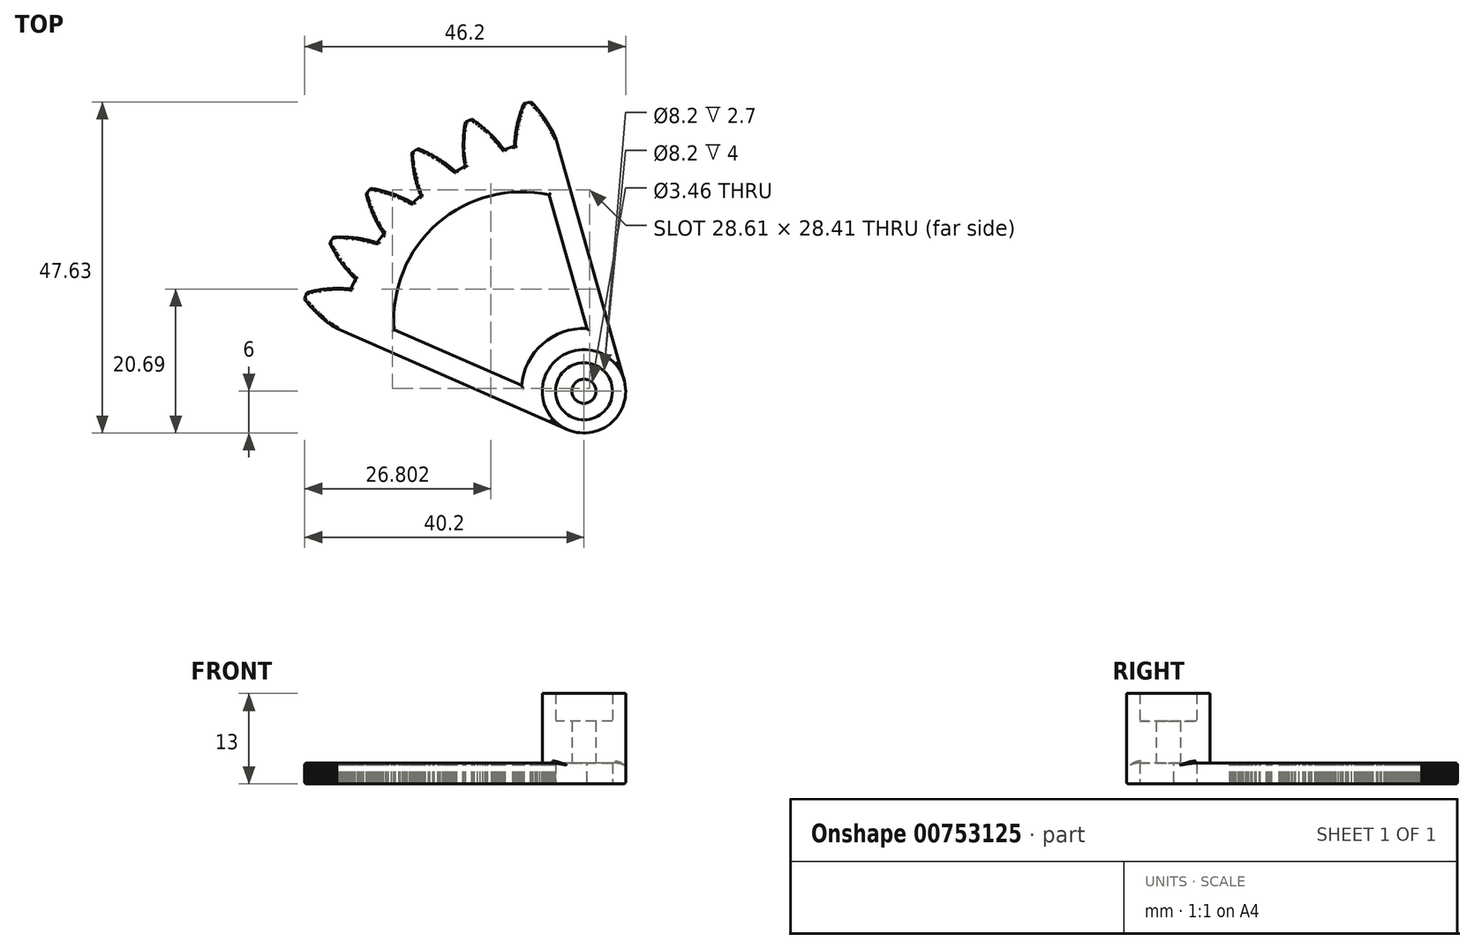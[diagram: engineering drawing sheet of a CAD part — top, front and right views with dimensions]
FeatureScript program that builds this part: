
annotation { "Feature Type Name" : "Feature", "Feature Type Description" : "" }
export const myFeature = defineFeature(function(context is Context, id is Id, definition is map)
    precondition{}
    {
        {
            var Q0;
            Q0=qCreatedBy(makeId("Top.planeOp"),FACE);
            var sketch = newSketch(context, id + "F0", { "sketchPlane" : qUnion([Q0])});
            skLineSegment(sketch, "E0", {"start": v(-4.1, 36.49) * mm, "end": v(-4.14, 36.6) * mm});
            skLineSegment(sketch, "E1", {"start": v(-4.23, 36.82) * mm, "end": v(-4.29, 36.94) * mm});
            skLineSegment(sketch, "E2", {"start": v(-4.29, 36.94) * mm, "end": v(-4.35, 37.07) * mm});
            skLineSegment(sketch, "E3", {"start": v(-4.35, 37.07) * mm, "end": v(-4.4, 37.2) * mm});
            skLineSegment(sketch, "E4", {"start": v(-4.4, 37.2) * mm, "end": v(-4.47, 37.33) * mm});
            skLineSegment(sketch, "E5", {"start": v(-4.47, 37.33) * mm, "end": v(-4.54, 37.46) * mm});
            skLineSegment(sketch, "E6", {"start": v(-4.54, 37.46) * mm, "end": v(-4.61, 37.6) * mm});
            skLineSegment(sketch, "E7", {"start": v(-4.61, 37.6) * mm, "end": v(-4.69, 37.74) * mm});
            skLineSegment(sketch, "E8", {"start": v(-4.69, 37.74) * mm, "end": v(-4.77, 37.88) * mm});
            skLineSegment(sketch, "E9", {"start": v(-4.77, 37.88) * mm, "end": v(-4.85, 38.03) * mm});
            skLineSegment(sketch, "E10", {"start": v(-4.85, 38.03) * mm, "end": v(-4.94, 38.18) * mm});
            skLineSegment(sketch, "E11", {"start": v(-4.94, 38.18) * mm, "end": v(-5.03, 38.34) * mm});
            skLineSegment(sketch, "E12", {"start": v(-5.03, 38.34) * mm, "end": v(-5.13, 38.5) * mm});
            skLineSegment(sketch, "E13", {"start": v(-5.13, 38.5) * mm, "end": v(-5.23, 38.65) * mm});
            skLineSegment(sketch, "E14", {"start": v(-5.23, 38.65) * mm, "end": v(-5.34, 38.81) * mm});
            skLineSegment(sketch, "E15", {"start": v(-5.34, 38.81) * mm, "end": v(-5.45, 38.98) * mm});
            skLineSegment(sketch, "E16", {"start": v(-5.45, 38.98) * mm, "end": v(-5.56, 39.15) * mm});
            skLineSegment(sketch, "E17", {"start": v(-5.56, 39.15) * mm, "end": v(-5.68, 39.32) * mm});
            skLineSegment(sketch, "E18", {"start": v(-5.68, 39.32) * mm, "end": v(-5.8, 39.5) * mm});
            skLineSegment(sketch, "E19", {"start": v(-5.8, 39.5) * mm, "end": v(-5.94, 39.67) * mm});
            skLineSegment(sketch, "E20", {"start": v(-5.94, 39.67) * mm, "end": v(-6.07, 39.84) * mm});
            skLineSegment(sketch, "E21", {"start": v(-6.07, 39.84) * mm, "end": v(-6.2, 40.03) * mm});
            skLineSegment(sketch, "E22", {"start": v(-6.2, 40.03) * mm, "end": v(-6.35, 40.2) * mm});
            skLineSegment(sketch, "E23", {"start": v(-6.35, 40.2) * mm, "end": v(-6.5, 40.4) * mm});
            skLineSegment(sketch, "E24", {"start": v(-6.5, 40.4) * mm, "end": v(-6.66, 40.58) * mm});
            skLineSegment(sketch, "E25", {"start": v(-6.66, 40.58) * mm, "end": v(-6.81, 40.77) * mm});
            skLineSegment(sketch, "E26", {"start": v(-6.81, 40.77) * mm, "end": v(-6.98, 40.96) * mm});
            skLineSegment(sketch, "E27", {"start": v(-6.98, 40.96) * mm, "end": v(-7.15, 41.15) * mm});
            skLineSegment(sketch, "E28", {"start": v(-7.15, 41.15) * mm, "end": v(-7.33, 41.34) * mm});
            skLineSegment(sketch, "E29", {"start": v(-7.33, 41.34) * mm, "end": v(-7.5, 41.53) * mm});
            skLineSegment(sketch, "E30", {"start": v(-7.5, 41.53) * mm, "end": v(-7.68, 41.63) * mm});
            skLineSegment(sketch, "E31", {"start": v(-7.68, 41.63) * mm, "end": v(-8.6, 41.45) * mm});
            skLineSegment(sketch, "E32", {"start": v(-8.6, 41.45) * mm, "end": v(-8.72, 41.3) * mm});
            skLineSegment(sketch, "E33", {"start": v(-8.72, 41.3) * mm, "end": v(-8.82, 41.05) * mm});
            skLineSegment(sketch, "E34", {"start": v(-8.82, 41.05) * mm, "end": v(-8.9, 40.8) * mm});
            skLineSegment(sketch, "E35", {"start": v(-8.9, 40.8) * mm, "end": v(-9, 40.56) * mm});
            skLineSegment(sketch, "E36", {"start": v(-9, 40.56) * mm, "end": v(-9.07, 40.32) * mm});
            skLineSegment(sketch, "E37", {"start": v(-9.07, 40.32) * mm, "end": v(-9.15, 40.09) * mm});
            skLineSegment(sketch, "E38", {"start": v(-9.15, 40.09) * mm, "end": v(-9.22, 39.86) * mm});
            skLineSegment(sketch, "E39", {"start": v(-9.22, 39.86) * mm, "end": v(-9.3, 39.63) * mm});
            skLineSegment(sketch, "E40", {"start": v(-9.3, 39.63) * mm, "end": v(-9.36, 39.4) * mm});
            skLineSegment(sketch, "E41", {"start": v(-9.36, 39.4) * mm, "end": v(-9.42, 39.19) * mm});
            skLineSegment(sketch, "E42", {"start": v(-9.42, 39.19) * mm, "end": v(-9.47, 38.97) * mm});
            skLineSegment(sketch, "E43", {"start": v(-9.47, 38.97) * mm, "end": v(-9.53, 38.76) * mm});
            skLineSegment(sketch, "E44", {"start": v(-9.53, 38.76) * mm, "end": v(-9.58, 38.55) * mm});
            skLineSegment(sketch, "E45", {"start": v(-9.58, 38.55) * mm, "end": v(-9.62, 38.35) * mm});
            skLineSegment(sketch, "E46", {"start": v(-9.62, 38.35) * mm, "end": v(-9.67, 38.15) * mm});
            skLineSegment(sketch, "E47", {"start": v(-9.67, 38.15) * mm, "end": v(-9.7, 37.96) * mm});
            skLineSegment(sketch, "E48", {"start": v(-9.7, 37.96) * mm, "end": v(-9.74, 37.77) * mm});
            skLineSegment(sketch, "E49", {"start": v(-9.74, 37.77) * mm, "end": v(-9.78, 37.58) * mm});
            skLineSegment(sketch, "E50", {"start": v(-9.78, 37.58) * mm, "end": v(-9.8, 37.4) * mm});
            skLineSegment(sketch, "E51", {"start": v(-9.8, 37.4) * mm, "end": v(-9.83, 37.22) * mm});
            skLineSegment(sketch, "E52", {"start": v(-9.83, 37.22) * mm, "end": v(-9.86, 37.05) * mm});
            skLineSegment(sketch, "E53", {"start": v(-9.86, 37.05) * mm, "end": v(-9.88, 36.88) * mm});
            skLineSegment(sketch, "E54", {"start": v(-9.88, 36.88) * mm, "end": v(-9.9, 36.72) * mm});
            skLineSegment(sketch, "E55", {"start": v(-9.9, 36.72) * mm, "end": v(-9.92, 36.56) * mm});
            skLineSegment(sketch, "E56", {"start": v(-9.92, 36.56) * mm, "end": v(-9.93, 36.4) * mm});
            skLineSegment(sketch, "E57", {"start": v(-9.93, 36.4) * mm, "end": v(-9.95, 36.25) * mm});
            skLineSegment(sketch, "E58", {"start": v(-9.95, 36.25) * mm, "end": v(-9.96, 36.1) * mm});
            skLineSegment(sketch, "E59", {"start": v(-9.96, 36.1) * mm, "end": v(-9.96, 35.97) * mm});
            skLineSegment(sketch, "E60", {"start": v(-9.96, 35.97) * mm, "end": v(-9.97, 35.83) * mm});
            skLineSegment(sketch, "E61", {"start": v(-9.97, 35.83) * mm, "end": v(-9.98, 35.7) * mm});
            skLineSegment(sketch, "E62", {"start": v(-9.98, 35.7) * mm, "end": v(-9.98, 35.57) * mm});
            skLineSegment(sketch, "E63", {"start": v(-9.98, 35.57) * mm, "end": v(-9.98, 35.45) * mm});
            skLineSegment(sketch, "E64", {"start": v(-9.98, 35.45) * mm, "end": v(-9.98, 35.33) * mm});
            skLineSegment(sketch, "E65", {"start": v(-9.98, 35.33) * mm, "end": v(-10.2, 35.2) * mm});
            skLineSegment(sketch, "E66", {"start": v(-10.2, 35.2) * mm, "end": v(-11.32, 34.85) * mm});
            skLineSegment(sketch, "E67", {"start": v(-11.32, 34.85) * mm, "end": v(-11.59, 34.84) * mm});
            skLineSegment(sketch, "E68", {"start": v(-11.59, 34.84) * mm, "end": v(-11.65, 34.93) * mm});
            skLineSegment(sketch, "E69", {"start": v(-11.65, 34.93) * mm, "end": v(-11.72, 35.04) * mm});
            skLineSegment(sketch, "E70", {"start": v(-11.72, 35.04) * mm, "end": v(-11.8, 35.14) * mm});
            skLineSegment(sketch, "E71", {"start": v(-11.8, 35.14) * mm, "end": v(-11.88, 35.24) * mm});
            skLineSegment(sketch, "E72", {"start": v(-11.88, 35.24) * mm, "end": v(-11.96, 35.35) * mm});
            skLineSegment(sketch, "E73", {"start": v(-11.96, 35.35) * mm, "end": v(-12.04, 35.47) * mm});
            skLineSegment(sketch, "E74", {"start": v(-12.04, 35.47) * mm, "end": v(-12.14, 35.58) * mm});
            skLineSegment(sketch, "E75", {"start": v(-12.14, 35.58) * mm, "end": v(-12.23, 35.7) * mm});
            skLineSegment(sketch, "E76", {"start": v(-12.23, 35.7) * mm, "end": v(-12.33, 35.82) * mm});
            skLineSegment(sketch, "E77", {"start": v(-12.33, 35.82) * mm, "end": v(-12.43, 35.94) * mm});
            skLineSegment(sketch, "E78", {"start": v(-12.43, 35.94) * mm, "end": v(-12.54, 36.06) * mm});
            skLineSegment(sketch, "E79", {"start": v(-12.54, 36.06) * mm, "end": v(-12.65, 36.2) * mm});
            skLineSegment(sketch, "E80", {"start": v(-12.65, 36.2) * mm, "end": v(-12.77, 36.32) * mm});
            skLineSegment(sketch, "E81", {"start": v(-12.77, 36.32) * mm, "end": v(-12.9, 36.45) * mm});
            skLineSegment(sketch, "E82", {"start": v(-12.9, 36.45) * mm, "end": v(-13.02, 36.58) * mm});
            skLineSegment(sketch, "E83", {"start": v(-13.02, 36.58) * mm, "end": v(-13.15, 36.72) * mm});
            skLineSegment(sketch, "E84", {"start": v(-13.15, 36.72) * mm, "end": v(-13.3, 36.86) * mm});
            skLineSegment(sketch, "E85", {"start": v(-13.3, 36.86) * mm, "end": v(-13.43, 37) * mm});
            skLineSegment(sketch, "E86", {"start": v(-13.43, 37) * mm, "end": v(-13.58, 37.14) * mm});
            skLineSegment(sketch, "E87", {"start": v(-13.58, 37.14) * mm, "end": v(-13.73, 37.28) * mm});
            skLineSegment(sketch, "E88", {"start": v(-13.73, 37.28) * mm, "end": v(-13.89, 37.42) * mm});
            skLineSegment(sketch, "E89", {"start": v(-13.89, 37.42) * mm, "end": v(-14.05, 37.57) * mm});
            skLineSegment(sketch, "E90", {"start": v(-14.05, 37.57) * mm, "end": v(-14.22, 37.71) * mm});
            skLineSegment(sketch, "E91", {"start": v(-14.22, 37.71) * mm, "end": v(-14.4, 37.86) * mm});
            skLineSegment(sketch, "E92", {"start": v(-14.4, 37.86) * mm, "end": v(-14.57, 38) * mm});
            skLineSegment(sketch, "E93", {"start": v(-14.57, 38) * mm, "end": v(-14.76, 38.16) * mm});
            skLineSegment(sketch, "E94", {"start": v(-14.76, 38.16) * mm, "end": v(-14.95, 38.3) * mm});
            skLineSegment(sketch, "E95", {"start": v(-14.95, 38.3) * mm, "end": v(-15.14, 38.46) * mm});
            skLineSegment(sketch, "E96", {"start": v(-15.14, 38.46) * mm, "end": v(-15.34, 38.6) * mm});
            skLineSegment(sketch, "E97", {"start": v(-15.34, 38.6) * mm, "end": v(-15.55, 38.76) * mm});
            skLineSegment(sketch, "E98", {"start": v(-15.55, 38.76) * mm, "end": v(-15.76, 38.91) * mm});
            skLineSegment(sketch, "E99", {"start": v(-15.76, 38.91) * mm, "end": v(-15.98, 39.06) * mm});
            skLineSegment(sketch, "E100", {"start": v(-15.98, 39.06) * mm, "end": v(-16.16, 39.13) * mm});
            skLineSegment(sketch, "E101", {"start": v(-16.16, 39.13) * mm, "end": v(-17.03, 38.75) * mm});
            skLineSegment(sketch, "E102", {"start": v(-17.03, 38.75) * mm, "end": v(-17.12, 38.58) * mm});
            skLineSegment(sketch, "E103", {"start": v(-17.12, 38.58) * mm, "end": v(-17.16, 38.32) * mm});
            skLineSegment(sketch, "E104", {"start": v(-17.16, 38.32) * mm, "end": v(-17.2, 38.06) * mm});
            skLineSegment(sketch, "E105", {"start": v(-17.2, 38.06) * mm, "end": v(-17.23, 37.8) * mm});
            skLineSegment(sketch, "E106", {"start": v(-17.23, 37.8) * mm, "end": v(-17.26, 37.55) * mm});
            skLineSegment(sketch, "E107", {"start": v(-17.26, 37.55) * mm, "end": v(-17.29, 37.3) * mm});
            skLineSegment(sketch, "E108", {"start": v(-17.29, 37.3) * mm, "end": v(-17.3, 37.07) * mm});
            skLineSegment(sketch, "E109", {"start": v(-17.3, 37.07) * mm, "end": v(-17.33, 36.83) * mm});
            skLineSegment(sketch, "E110", {"start": v(-17.33, 36.83) * mm, "end": v(-17.35, 36.6) * mm});
            skLineSegment(sketch, "E111", {"start": v(-17.35, 36.6) * mm, "end": v(-17.36, 36.37) * mm});
            skLineSegment(sketch, "E112", {"start": v(-17.36, 36.37) * mm, "end": v(-17.37, 36.15) * mm});
            skLineSegment(sketch, "E113", {"start": v(-17.37, 36.15) * mm, "end": v(-17.38, 35.93) * mm});
            skLineSegment(sketch, "E114", {"start": v(-17.38, 35.93) * mm, "end": v(-17.38, 35.72) * mm});
            skLineSegment(sketch, "E115", {"start": v(-17.38, 35.72) * mm, "end": v(-17.39, 35.51) * mm});
            skLineSegment(sketch, "E116", {"start": v(-17.39, 35.51) * mm, "end": v(-17.39, 35.3) * mm});
            skLineSegment(sketch, "E117", {"start": v(-17.39, 35.3) * mm, "end": v(-17.39, 35.11) * mm});
            skLineSegment(sketch, "E118", {"start": v(-17.39, 35.11) * mm, "end": v(-17.38, 34.92) * mm});
            skLineSegment(sketch, "E119", {"start": v(-17.38, 34.92) * mm, "end": v(-17.38, 34.73) * mm});
            skLineSegment(sketch, "E120", {"start": v(-17.38, 34.73) * mm, "end": v(-17.37, 34.54) * mm});
            skLineSegment(sketch, "E121", {"start": v(-17.37, 34.54) * mm, "end": v(-17.36, 34.36) * mm});
            skLineSegment(sketch, "E122", {"start": v(-17.36, 34.36) * mm, "end": v(-17.35, 34.2) * mm});
            skLineSegment(sketch, "E123", {"start": v(-17.35, 34.2) * mm, "end": v(-17.33, 34.02) * mm});
            skLineSegment(sketch, "E124", {"start": v(-17.33, 34.02) * mm, "end": v(-17.32, 33.86) * mm});
            skLineSegment(sketch, "E125", {"start": v(-17.32, 33.86) * mm, "end": v(-17.3, 33.7) * mm});
            skLineSegment(sketch, "E126", {"start": v(-17.3, 33.7) * mm, "end": v(-17.28, 33.54) * mm});
            skLineSegment(sketch, "E127", {"start": v(-17.28, 33.54) * mm, "end": v(-17.27, 33.4) * mm});
            skLineSegment(sketch, "E128", {"start": v(-17.27, 33.4) * mm, "end": v(-17.25, 33.25) * mm});
            skLineSegment(sketch, "E129", {"start": v(-17.25, 33.25) * mm, "end": v(-17.22, 33.1) * mm});
            skLineSegment(sketch, "E130", {"start": v(-17.22, 33.1) * mm, "end": v(-17.2, 32.97) * mm});
            skLineSegment(sketch, "E131", {"start": v(-17.2, 32.97) * mm, "end": v(-17.18, 32.84) * mm});
            skLineSegment(sketch, "E132", {"start": v(-17.18, 32.84) * mm, "end": v(-17.16, 32.72) * mm});
            skLineSegment(sketch, "E133", {"start": v(-17.16, 32.72) * mm, "end": v(-17.13, 32.6) * mm});
            skLineSegment(sketch, "E134", {"start": v(-17.13, 32.6) * mm, "end": v(-17.1, 32.48) * mm});
            skLineSegment(sketch, "E135", {"start": v(-17.1, 32.48) * mm, "end": v(-17.3, 32.3) * mm});
            skLineSegment(sketch, "E136", {"start": v(-17.3, 32.3) * mm, "end": v(-18.32, 31.73) * mm});
            skLineSegment(sketch, "E137", {"start": v(-18.32, 31.73) * mm, "end": v(-18.58, 31.67) * mm});
            skLineSegment(sketch, "E138", {"start": v(-18.58, 31.67) * mm, "end": v(-18.66, 31.75) * mm});
            skLineSegment(sketch, "E139", {"start": v(-18.66, 31.75) * mm, "end": v(-18.75, 31.83) * mm});
            skLineSegment(sketch, "E140", {"start": v(-18.75, 31.83) * mm, "end": v(-18.85, 31.92) * mm});
            skLineSegment(sketch, "E141", {"start": v(-18.85, 31.92) * mm, "end": v(-18.94, 32) * mm});
            skLineSegment(sketch, "E142", {"start": v(-18.94, 32) * mm, "end": v(-19.05, 32.1) * mm});
            skLineSegment(sketch, "E143", {"start": v(-19.05, 32.1) * mm, "end": v(-19.15, 32.19) * mm});
            skLineSegment(sketch, "E144", {"start": v(-19.15, 32.19) * mm, "end": v(-19.27, 32.28) * mm});
            skLineSegment(sketch, "E145", {"start": v(-19.27, 32.28) * mm, "end": v(-19.38, 32.37) * mm});
            skLineSegment(sketch, "E146", {"start": v(-19.38, 32.37) * mm, "end": v(-19.5, 32.47) * mm});
            skLineSegment(sketch, "E147", {"start": v(-19.5, 32.47) * mm, "end": v(-19.63, 32.57) * mm});
            skLineSegment(sketch, "E148", {"start": v(-19.63, 32.57) * mm, "end": v(-19.77, 32.67) * mm});
            skLineSegment(sketch, "E149", {"start": v(-19.77, 32.67) * mm, "end": v(-19.9, 32.77) * mm});
            skLineSegment(sketch, "E150", {"start": v(-19.9, 32.77) * mm, "end": v(-20.04, 32.87) * mm});
            skLineSegment(sketch, "E151", {"start": v(-20.04, 32.87) * mm, "end": v(-20.2, 32.97) * mm});
            skLineSegment(sketch, "E152", {"start": v(-20.2, 32.97) * mm, "end": v(-20.34, 33.08) * mm});
            skLineSegment(sketch, "E153", {"start": v(-20.34, 33.08) * mm, "end": v(-20.5, 33.18) * mm});
            skLineSegment(sketch, "E154", {"start": v(-20.5, 33.18) * mm, "end": v(-20.66, 33.29) * mm});
            skLineSegment(sketch, "E155", {"start": v(-20.66, 33.29) * mm, "end": v(-20.83, 33.4) * mm});
            skLineSegment(sketch, "E156", {"start": v(-20.83, 33.4) * mm, "end": v(-21, 33.5) * mm});
            skLineSegment(sketch, "E157", {"start": v(-21, 33.5) * mm, "end": v(-21.18, 33.6) * mm});
            skLineSegment(sketch, "E158", {"start": v(-21.18, 33.6) * mm, "end": v(-21.37, 33.72) * mm});
            skLineSegment(sketch, "E159", {"start": v(-21.37, 33.72) * mm, "end": v(-21.56, 33.82) * mm});
            skLineSegment(sketch, "E160", {"start": v(-21.56, 33.82) * mm, "end": v(-21.75, 33.93) * mm});
            skLineSegment(sketch, "E161", {"start": v(-21.75, 33.93) * mm, "end": v(-21.95, 34.04) * mm});
            skLineSegment(sketch, "E162", {"start": v(-21.95, 34.04) * mm, "end": v(-22.16, 34.15) * mm});
            skLineSegment(sketch, "E163", {"start": v(-22.16, 34.15) * mm, "end": v(-22.37, 34.26) * mm});
            skLineSegment(sketch, "E164", {"start": v(-22.37, 34.26) * mm, "end": v(-22.58, 34.36) * mm});
            skLineSegment(sketch, "E165", {"start": v(-22.58, 34.36) * mm, "end": v(-22.8, 34.47) * mm});
            skLineSegment(sketch, "E166", {"start": v(-22.8, 34.47) * mm, "end": v(-23.03, 34.58) * mm});
            skLineSegment(sketch, "E167", {"start": v(-23.03, 34.58) * mm, "end": v(-23.27, 34.68) * mm});
            skLineSegment(sketch, "E168", {"start": v(-23.27, 34.68) * mm, "end": v(-23.5, 34.79) * mm});
            skLineSegment(sketch, "E169", {"start": v(-23.5, 34.79) * mm, "end": v(-23.75, 34.89) * mm});
            skLineSegment(sketch, "E170", {"start": v(-23.75, 34.89) * mm, "end": v(-23.94, 34.9) * mm});
            skLineSegment(sketch, "E171", {"start": v(-23.94, 34.9) * mm, "end": v(-24.72, 34.37) * mm});
            skLineSegment(sketch, "E172", {"start": v(-24.72, 34.37) * mm, "end": v(-24.76, 34.18) * mm});
            skLineSegment(sketch, "E173", {"start": v(-24.76, 34.18) * mm, "end": v(-24.75, 33.91) * mm});
            skLineSegment(sketch, "E174", {"start": v(-24.75, 33.91) * mm, "end": v(-24.73, 33.65) * mm});
            skLineSegment(sketch, "E175", {"start": v(-24.73, 33.65) * mm, "end": v(-24.71, 33.4) * mm});
            skLineSegment(sketch, "E176", {"start": v(-24.71, 33.4) * mm, "end": v(-24.7, 33.15) * mm});
            skLineSegment(sketch, "E177", {"start": v(-24.7, 33.15) * mm, "end": v(-24.67, 32.9) * mm});
            skLineSegment(sketch, "E178", {"start": v(-24.67, 32.9) * mm, "end": v(-24.64, 32.66) * mm});
            skLineSegment(sketch, "E179", {"start": v(-24.64, 32.66) * mm, "end": v(-24.6, 32.43) * mm});
            skLineSegment(sketch, "E180", {"start": v(-24.6, 32.43) * mm, "end": v(-24.58, 32.2) * mm});
            skLineSegment(sketch, "E181", {"start": v(-24.58, 32.2) * mm, "end": v(-24.54, 31.97) * mm});
            skLineSegment(sketch, "E182", {"start": v(-24.54, 31.97) * mm, "end": v(-24.5, 31.75) * mm});
            skLineSegment(sketch, "E183", {"start": v(-24.5, 31.75) * mm, "end": v(-24.47, 31.54) * mm});
            skLineSegment(sketch, "E184", {"start": v(-24.47, 31.54) * mm, "end": v(-24.43, 31.33) * mm});
            skLineSegment(sketch, "E185", {"start": v(-24.43, 31.33) * mm, "end": v(-24.4, 31.12) * mm});
            skLineSegment(sketch, "E186", {"start": v(-24.4, 31.12) * mm, "end": v(-24.35, 30.92) * mm});
            skLineSegment(sketch, "E187", {"start": v(-24.35, 30.92) * mm, "end": v(-24.3, 30.73) * mm});
            skLineSegment(sketch, "E188", {"start": v(-24.3, 30.73) * mm, "end": v(-24.26, 30.54) * mm});
            skLineSegment(sketch, "E189", {"start": v(-24.26, 30.54) * mm, "end": v(-24.22, 30.36) * mm});
            skLineSegment(sketch, "E190", {"start": v(-24.22, 30.36) * mm, "end": v(-24.17, 30.18) * mm});
            skLineSegment(sketch, "E191", {"start": v(-24.17, 30.18) * mm, "end": v(-24.12, 30) * mm});
            skLineSegment(sketch, "E192", {"start": v(-24.12, 30) * mm, "end": v(-24.08, 29.84) * mm});
            skLineSegment(sketch, "E193", {"start": v(-24.08, 29.84) * mm, "end": v(-24.03, 29.67) * mm});
            skLineSegment(sketch, "E194", {"start": v(-24.03, 29.67) * mm, "end": v(-23.98, 29.52) * mm});
            skLineSegment(sketch, "E195", {"start": v(-23.98, 29.52) * mm, "end": v(-23.93, 29.36) * mm});
            skLineSegment(sketch, "E196", {"start": v(-23.93, 29.36) * mm, "end": v(-23.88, 29.22) * mm});
            skLineSegment(sketch, "E197", {"start": v(-23.88, 29.22) * mm, "end": v(-23.83, 29.07) * mm});
            skLineSegment(sketch, "E198", {"start": v(-23.83, 29.07) * mm, "end": v(-23.78, 28.94) * mm});
            skLineSegment(sketch, "E199", {"start": v(-23.78, 28.94) * mm, "end": v(-23.73, 28.8) * mm});
            skLineSegment(sketch, "E200", {"start": v(-23.73, 28.8) * mm, "end": v(-23.68, 28.68) * mm});
            skLineSegment(sketch, "E201", {"start": v(-23.68, 28.68) * mm, "end": v(-23.63, 28.55) * mm});
            skLineSegment(sketch, "E202", {"start": v(-23.63, 28.55) * mm, "end": v(-23.59, 28.44) * mm});
            skLineSegment(sketch, "E203", {"start": v(-23.59, 28.44) * mm, "end": v(-23.54, 28.32) * mm});
            skLineSegment(sketch, "E204", {"start": v(-23.54, 28.32) * mm, "end": v(-23.5, 28.22) * mm});
            skLineSegment(sketch, "E205", {"start": v(-23.5, 28.22) * mm, "end": v(-23.64, 28) * mm});
            skLineSegment(sketch, "E206", {"start": v(-23.64, 28) * mm, "end": v(-24.52, 27.23) * mm});
            skLineSegment(sketch, "E207", {"start": v(-24.52, 27.23) * mm, "end": v(-24.76, 27.11) * mm});
            skLineSegment(sketch, "E208", {"start": v(-24.76, 27.11) * mm, "end": v(-24.86, 27.17) * mm});
            skLineSegment(sketch, "E209", {"start": v(-24.86, 27.17) * mm, "end": v(-24.96, 27.24) * mm});
            skLineSegment(sketch, "E210", {"start": v(-24.96, 27.24) * mm, "end": v(-25.07, 27.3) * mm});
            skLineSegment(sketch, "E211", {"start": v(-25.07, 27.3) * mm, "end": v(-25.18, 27.37) * mm});
            skLineSegment(sketch, "E212", {"start": v(-25.18, 27.37) * mm, "end": v(-25.3, 27.43) * mm});
            skLineSegment(sketch, "E213", {"start": v(-25.3, 27.43) * mm, "end": v(-25.43, 27.5) * mm});
            skLineSegment(sketch, "E214", {"start": v(-25.43, 27.5) * mm, "end": v(-25.56, 27.57) * mm});
            skLineSegment(sketch, "E215", {"start": v(-25.56, 27.57) * mm, "end": v(-25.7, 27.64) * mm});
            skLineSegment(sketch, "E216", {"start": v(-25.7, 27.64) * mm, "end": v(-25.83, 27.7) * mm});
            skLineSegment(sketch, "E217", {"start": v(-25.83, 27.7) * mm, "end": v(-25.98, 27.77) * mm});
            skLineSegment(sketch, "E218", {"start": v(-25.98, 27.77) * mm, "end": v(-26.12, 27.84) * mm});
            skLineSegment(sketch, "E219", {"start": v(-26.12, 27.84) * mm, "end": v(-26.28, 27.91) * mm});
            skLineSegment(sketch, "E220", {"start": v(-26.28, 27.91) * mm, "end": v(-26.44, 27.99) * mm});
            skLineSegment(sketch, "E221", {"start": v(-26.44, 27.99) * mm, "end": v(-26.6, 28.06) * mm});
            skLineSegment(sketch, "E222", {"start": v(-26.6, 28.06) * mm, "end": v(-26.78, 28.12) * mm});
            skLineSegment(sketch, "E223", {"start": v(-26.78, 28.12) * mm, "end": v(-26.95, 28.2) * mm});
            skLineSegment(sketch, "E224", {"start": v(-26.95, 28.2) * mm, "end": v(-27.13, 28.26) * mm});
            skLineSegment(sketch, "E225", {"start": v(-27.13, 28.26) * mm, "end": v(-27.32, 28.33) * mm});
            skLineSegment(sketch, "E226", {"start": v(-27.32, 28.33) * mm, "end": v(-27.5, 28.4) * mm});
            skLineSegment(sketch, "E227", {"start": v(-27.5, 28.4) * mm, "end": v(-27.7, 28.47) * mm});
            skLineSegment(sketch, "E228", {"start": v(-27.7, 28.47) * mm, "end": v(-27.9, 28.54) * mm});
            skLineSegment(sketch, "E229", {"start": v(-27.9, 28.54) * mm, "end": v(-28.12, 28.6) * mm});
            skLineSegment(sketch, "E230", {"start": v(-28.12, 28.6) * mm, "end": v(-28.33, 28.67) * mm});
            skLineSegment(sketch, "E231", {"start": v(-28.33, 28.67) * mm, "end": v(-28.55, 28.73) * mm});
            skLineSegment(sketch, "E232", {"start": v(-28.55, 28.73) * mm, "end": v(-28.77, 28.8) * mm});
            skLineSegment(sketch, "E233", {"start": v(-28.77, 28.8) * mm, "end": v(-29, 28.86) * mm});
            skLineSegment(sketch, "E234", {"start": v(-29, 28.86) * mm, "end": v(-29.24, 28.92) * mm});
            skLineSegment(sketch, "E235", {"start": v(-29.24, 28.92) * mm, "end": v(-29.47, 28.97) * mm});
            skLineSegment(sketch, "E236", {"start": v(-29.47, 28.97) * mm, "end": v(-29.72, 29.03) * mm});
            skLineSegment(sketch, "E237", {"start": v(-29.72, 29.03) * mm, "end": v(-29.97, 29.08) * mm});
            skLineSegment(sketch, "E238", {"start": v(-29.97, 29.08) * mm, "end": v(-30.22, 29.14) * mm});
            skLineSegment(sketch, "E239", {"start": v(-30.22, 29.14) * mm, "end": v(-30.49, 29.19) * mm});
            skLineSegment(sketch, "E240", {"start": v(-30.49, 29.19) * mm, "end": v(-30.68, 29.17) * mm});
            skLineSegment(sketch, "E241", {"start": v(-30.68, 29.17) * mm, "end": v(-31.32, 28.48) * mm});
            skLineSegment(sketch, "E242", {"start": v(-31.32, 28.48) * mm, "end": v(-31.33, 28.28) * mm});
            skLineSegment(sketch, "E243", {"start": v(-31.33, 28.28) * mm, "end": v(-31.26, 28.02) * mm});
            skLineSegment(sketch, "E244", {"start": v(-31.26, 28.02) * mm, "end": v(-31.19, 27.77) * mm});
            skLineSegment(sketch, "E245", {"start": v(-31.19, 27.77) * mm, "end": v(-31.12, 27.53) * mm});
            skLineSegment(sketch, "E246", {"start": v(-31.12, 27.53) * mm, "end": v(-31.04, 27.29) * mm});
            skLineSegment(sketch, "E247", {"start": v(-31.04, 27.29) * mm, "end": v(-30.97, 27.05) * mm});
            skLineSegment(sketch, "E248", {"start": v(-30.97, 27.05) * mm, "end": v(-30.9, 26.82) * mm});
            skLineSegment(sketch, "E249", {"start": v(-30.9, 26.82) * mm, "end": v(-30.81, 26.6) * mm});
            skLineSegment(sketch, "E250", {"start": v(-30.81, 26.6) * mm, "end": v(-30.73, 26.38) * mm});
            skLineSegment(sketch, "E251", {"start": v(-30.73, 26.38) * mm, "end": v(-30.65, 26.17) * mm});
            skLineSegment(sketch, "E252", {"start": v(-30.65, 26.17) * mm, "end": v(-30.57, 25.96) * mm});
            skLineSegment(sketch, "E253", {"start": v(-30.57, 25.96) * mm, "end": v(-30.5, 25.76) * mm});
            skLineSegment(sketch, "E254", {"start": v(-30.5, 25.76) * mm, "end": v(-30.41, 25.56) * mm});
            skLineSegment(sketch, "E255", {"start": v(-30.41, 25.56) * mm, "end": v(-30.33, 25.37) * mm});
            skLineSegment(sketch, "E256", {"start": v(-30.33, 25.37) * mm, "end": v(-30.25, 25.19) * mm});
            skLineSegment(sketch, "E257", {"start": v(-30.25, 25.19) * mm, "end": v(-30.16, 25) * mm});
            skLineSegment(sketch, "E258", {"start": v(-30.16, 25) * mm, "end": v(-30.08, 24.83) * mm});
            skLineSegment(sketch, "E259", {"start": v(-30.08, 24.83) * mm, "end": v(-30, 24.66) * mm});
            skLineSegment(sketch, "E260", {"start": v(-30, 24.66) * mm, "end": v(-29.92, 24.5) * mm});
            skLineSegment(sketch, "E261", {"start": v(-29.92, 24.5) * mm, "end": v(-29.83, 24.33) * mm});
            skLineSegment(sketch, "E262", {"start": v(-29.83, 24.33) * mm, "end": v(-29.75, 24.18) * mm});
            skLineSegment(sketch, "E263", {"start": v(-29.75, 24.18) * mm, "end": v(-29.67, 24.03) * mm});
            skLineSegment(sketch, "E264", {"start": v(-29.67, 24.03) * mm, "end": v(-29.6, 23.89) * mm});
            skLineSegment(sketch, "E265", {"start": v(-29.6, 23.89) * mm, "end": v(-29.51, 23.75) * mm});
            skLineSegment(sketch, "E266", {"start": v(-29.51, 23.75) * mm, "end": v(-29.43, 23.61) * mm});
            skLineSegment(sketch, "E267", {"start": v(-29.43, 23.61) * mm, "end": v(-29.36, 23.48) * mm});
            skLineSegment(sketch, "E268", {"start": v(-29.36, 23.48) * mm, "end": v(-29.28, 23.36) * mm});
            skLineSegment(sketch, "E269", {"start": v(-29.28, 23.36) * mm, "end": v(-29.2, 23.24) * mm});
            skLineSegment(sketch, "E270", {"start": v(-29.2, 23.24) * mm, "end": v(-29.13, 23.13) * mm});
            skLineSegment(sketch, "E271", {"start": v(-29.13, 23.13) * mm, "end": v(-29.05, 23.02) * mm});
            skLineSegment(sketch, "E272", {"start": v(-29.05, 23.02) * mm, "end": v(-28.98, 22.91) * mm});
            skLineSegment(sketch, "E273", {"start": v(-28.98, 22.91) * mm, "end": v(-28.91, 22.81) * mm});
            skLineSegment(sketch, "E274", {"start": v(-28.91, 22.81) * mm, "end": v(-28.84, 22.72) * mm});
            skLineSegment(sketch, "E275", {"start": v(-28.84, 22.72) * mm, "end": v(-28.94, 22.47) * mm});
            skLineSegment(sketch, "E276", {"start": v(-28.94, 22.47) * mm, "end": v(-29.65, 21.54) * mm});
            skLineSegment(sketch, "E277", {"start": v(-29.65, 21.54) * mm, "end": v(-29.85, 21.37) * mm});
            skLineSegment(sketch, "E278", {"start": v(-29.85, 21.37) * mm, "end": v(-29.96, 21.41) * mm});
            skLineSegment(sketch, "E279", {"start": v(-29.96, 21.41) * mm, "end": v(-30.08, 21.45) * mm});
            skLineSegment(sketch, "E280", {"start": v(-30.08, 21.45) * mm, "end": v(-30.2, 21.5) * mm});
            skLineSegment(sketch, "E281", {"start": v(-30.2, 21.5) * mm, "end": v(-30.32, 21.53) * mm});
            skLineSegment(sketch, "E282", {"start": v(-30.32, 21.53) * mm, "end": v(-30.45, 21.57) * mm});
            skLineSegment(sketch, "E283", {"start": v(-30.45, 21.57) * mm, "end": v(-30.59, 21.61) * mm});
            skLineSegment(sketch, "E284", {"start": v(-30.59, 21.61) * mm, "end": v(-30.73, 21.65) * mm});
            skLineSegment(sketch, "E285", {"start": v(-30.73, 21.65) * mm, "end": v(-30.88, 21.7) * mm});
            skLineSegment(sketch, "E286", {"start": v(-30.88, 21.7) * mm, "end": v(-31.03, 21.73) * mm});
            skLineSegment(sketch, "E287", {"start": v(-31.03, 21.73) * mm, "end": v(-31.18, 21.77) * mm});
            skLineSegment(sketch, "E288", {"start": v(-31.18, 21.77) * mm, "end": v(-31.34, 21.8) * mm});
            skLineSegment(sketch, "E289", {"start": v(-31.34, 21.8) * mm, "end": v(-31.5, 21.84) * mm});
            skLineSegment(sketch, "E290", {"start": v(-31.5, 21.84) * mm, "end": v(-31.68, 21.88) * mm});
            skLineSegment(sketch, "E291", {"start": v(-31.68, 21.88) * mm, "end": v(-31.86, 21.91) * mm});
            skLineSegment(sketch, "E292", {"start": v(-31.86, 21.91) * mm, "end": v(-32.04, 21.94) * mm});
            skLineSegment(sketch, "E293", {"start": v(-32.04, 21.94) * mm, "end": v(-32.22, 21.98) * mm});
            skLineSegment(sketch, "E294", {"start": v(-32.22, 21.98) * mm, "end": v(-32.42, 22) * mm});
            skLineSegment(sketch, "E295", {"start": v(-32.42, 22) * mm, "end": v(-32.61, 22.03) * mm});
            skLineSegment(sketch, "E296", {"start": v(-32.61, 22.03) * mm, "end": v(-32.81, 22.06) * mm});
            skLineSegment(sketch, "E297", {"start": v(-32.81, 22.06) * mm, "end": v(-33.02, 22.09) * mm});
            skLineSegment(sketch, "E298", {"start": v(-33.02, 22.09) * mm, "end": v(-33.23, 22.11) * mm});
            skLineSegment(sketch, "E299", {"start": v(-33.23, 22.11) * mm, "end": v(-33.45, 22.13) * mm});
            skLineSegment(sketch, "E300", {"start": v(-33.45, 22.13) * mm, "end": v(-33.67, 22.15) * mm});
            skLineSegment(sketch, "E301", {"start": v(-33.67, 22.15) * mm, "end": v(-33.9, 22.17) * mm});
            skLineSegment(sketch, "E302", {"start": v(-33.9, 22.17) * mm, "end": v(-34.13, 22.18) * mm});
            skLineSegment(sketch, "E303", {"start": v(-34.13, 22.18) * mm, "end": v(-34.37, 22.2) * mm});
            skLineSegment(sketch, "E304", {"start": v(-34.37, 22.2) * mm, "end": v(-34.6, 22.2) * mm});
            skLineSegment(sketch, "E305", {"start": v(-34.6, 22.2) * mm, "end": v(-34.85, 22.21) * mm});
            skLineSegment(sketch, "E306", {"start": v(-34.85, 22.21) * mm, "end": v(-35.1, 22.22) * mm});
            skLineSegment(sketch, "E307", {"start": v(-35.1, 22.22) * mm, "end": v(-35.36, 22.22) * mm});
            skLineSegment(sketch, "E308", {"start": v(-35.36, 22.22) * mm, "end": v(-35.62, 22.22) * mm});
            skLineSegment(sketch, "E309", {"start": v(-35.62, 22.22) * mm, "end": v(-35.89, 22.21) * mm});
            skLineSegment(sketch, "E310", {"start": v(-35.89, 22.21) * mm, "end": v(-36.07, 22.15) * mm});
            skLineSegment(sketch, "E311", {"start": v(-36.07, 22.15) * mm, "end": v(-36.56, 21.34) * mm});
            skLineSegment(sketch, "E312", {"start": v(-36.56, 21.34) * mm, "end": v(-36.53, 21.15) * mm});
            skLineSegment(sketch, "E313", {"start": v(-36.53, 21.15) * mm, "end": v(-36.4, 20.91) * mm});
            skLineSegment(sketch, "E314", {"start": v(-36.4, 20.91) * mm, "end": v(-36.28, 20.68) * mm});
            skLineSegment(sketch, "E315", {"start": v(-36.28, 20.68) * mm, "end": v(-36.16, 20.46) * mm});
            skLineSegment(sketch, "E316", {"start": v(-36.16, 20.46) * mm, "end": v(-36.04, 20.24) * mm});
            skLineSegment(sketch, "E317", {"start": v(-36.04, 20.24) * mm, "end": v(-35.91, 20.02) * mm});
            skLineSegment(sketch, "E318", {"start": v(-35.91, 20.02) * mm, "end": v(-35.8, 19.81) * mm});
            skLineSegment(sketch, "E319", {"start": v(-35.8, 19.81) * mm, "end": v(-35.67, 19.61) * mm});
            skLineSegment(sketch, "E320", {"start": v(-35.67, 19.61) * mm, "end": v(-35.55, 19.42) * mm});
            skLineSegment(sketch, "E321", {"start": v(-35.55, 19.42) * mm, "end": v(-35.42, 19.22) * mm});
            skLineSegment(sketch, "E322", {"start": v(-35.42, 19.22) * mm, "end": v(-35.3, 19.04) * mm});
            skLineSegment(sketch, "E323", {"start": v(-35.3, 19.04) * mm, "end": v(-35.18, 18.86) * mm});
            skLineSegment(sketch, "E324", {"start": v(-35.18, 18.86) * mm, "end": v(-35.06, 18.68) * mm});
            skLineSegment(sketch, "E325", {"start": v(-35.06, 18.68) * mm, "end": v(-34.94, 18.51) * mm});
            skLineSegment(sketch, "E326", {"start": v(-34.94, 18.51) * mm, "end": v(-34.82, 18.35) * mm});
            skLineSegment(sketch, "E327", {"start": v(-34.82, 18.35) * mm, "end": v(-34.7, 18.19) * mm});
            skLineSegment(sketch, "E328", {"start": v(-34.7, 18.19) * mm, "end": v(-34.59, 18.03) * mm});
            skLineSegment(sketch, "E329", {"start": v(-34.59, 18.03) * mm, "end": v(-34.47, 17.88) * mm});
            skLineSegment(sketch, "E330", {"start": v(-34.47, 17.88) * mm, "end": v(-34.36, 17.74) * mm});
            skLineSegment(sketch, "E331", {"start": v(-34.36, 17.74) * mm, "end": v(-34.24, 17.6) * mm});
            skLineSegment(sketch, "E332", {"start": v(-34.24, 17.6) * mm, "end": v(-34.13, 17.46) * mm});
            skLineSegment(sketch, "E333", {"start": v(-34.13, 17.46) * mm, "end": v(-34.02, 17.34) * mm});
            skLineSegment(sketch, "E334", {"start": v(-34.02, 17.34) * mm, "end": v(-33.91, 17.21) * mm});
            skLineSegment(sketch, "E335", {"start": v(-33.91, 17.21) * mm, "end": v(-33.8, 17.1) * mm});
            skLineSegment(sketch, "E336", {"start": v(-33.8, 17.1) * mm, "end": v(-33.7, 16.98) * mm});
            skLineSegment(sketch, "E337", {"start": v(-33.7, 16.98) * mm, "end": v(-33.6, 16.87) * mm});
            skLineSegment(sketch, "E338", {"start": v(-33.6, 16.87) * mm, "end": v(-33.5, 16.76) * mm});
            skLineSegment(sketch, "E339", {"start": v(-33.5, 16.76) * mm, "end": v(-33.4, 16.66) * mm});
            skLineSegment(sketch, "E340", {"start": v(-33.4, 16.66) * mm, "end": v(-33.3, 16.56) * mm});
            skLineSegment(sketch, "E341", {"start": v(-33.3, 16.56) * mm, "end": v(-33.2, 16.47) * mm});
            skLineSegment(sketch, "E342", {"start": v(-33.2, 16.47) * mm, "end": v(-33.11, 16.38) * mm});
            skLineSegment(sketch, "E343", {"start": v(-33.11, 16.38) * mm, "end": v(-33.02, 16.3) * mm});
            skLineSegment(sketch, "E344", {"start": v(-33.02, 16.3) * mm, "end": v(-32.94, 16.22) * mm});
            skLineSegment(sketch, "E345", {"start": v(-32.94, 16.22) * mm, "end": v(-32.98, 15.96) * mm});
            skLineSegment(sketch, "E346", {"start": v(-32.98, 15.96) * mm, "end": v(-33.48, 14.9) * mm});
            skLineSegment(sketch, "E347", {"start": v(-33.48, 14.9) * mm, "end": v(-33.64, 14.7) * mm});
            skLineSegment(sketch, "E348", {"start": v(-33.64, 14.7) * mm, "end": v(-33.76, 14.72) * mm});
            skLineSegment(sketch, "E349", {"start": v(-33.76, 14.72) * mm, "end": v(-33.88, 14.73) * mm});
            skLineSegment(sketch, "E350", {"start": v(-33.88, 14.73) * mm, "end": v(-34, 14.75) * mm});
            skLineSegment(sketch, "E351", {"start": v(-34, 14.75) * mm, "end": v(-34.14, 14.76) * mm});
            skLineSegment(sketch, "E352", {"start": v(-34.14, 14.76) * mm, "end": v(-34.27, 14.77) * mm});
            skLineSegment(sketch, "E353", {"start": v(-34.27, 14.77) * mm, "end": v(-34.42, 14.78) * mm});
            skLineSegment(sketch, "E354", {"start": v(-34.42, 14.78) * mm, "end": v(-34.56, 14.79) * mm});
            skLineSegment(sketch, "E355", {"start": v(-34.56, 14.79) * mm, "end": v(-34.71, 14.8) * mm});
            skLineSegment(sketch, "E356", {"start": v(-34.71, 14.8) * mm, "end": v(-34.87, 14.8) * mm});
            skLineSegment(sketch, "E357", {"start": v(-34.87, 14.8) * mm, "end": v(-35.03, 14.8) * mm});
            skLineSegment(sketch, "E358", {"start": v(-35.03, 14.8) * mm, "end": v(-35.2, 14.81) * mm});
            skLineSegment(sketch, "E359", {"start": v(-35.2, 14.81) * mm, "end": v(-35.36, 14.81) * mm});
            skLineSegment(sketch, "E360", {"start": v(-35.36, 14.81) * mm, "end": v(-35.54, 14.81) * mm});
            skLineSegment(sketch, "E361", {"start": v(-35.54, 14.81) * mm, "end": v(-35.72, 14.8) * mm});
            skLineSegment(sketch, "E362", {"start": v(-35.72, 14.8) * mm, "end": v(-35.9, 14.8) * mm});
            skLineSegment(sketch, "E363", {"start": v(-35.9, 14.8) * mm, "end": v(-36.09, 14.8) * mm});
            skLineSegment(sketch, "E364", {"start": v(-36.09, 14.8) * mm, "end": v(-36.28, 14.78) * mm});
            skLineSegment(sketch, "E365", {"start": v(-36.28, 14.78) * mm, "end": v(-36.48, 14.77) * mm});
            skLineSegment(sketch, "E366", {"start": v(-36.48, 14.77) * mm, "end": v(-36.68, 14.76) * mm});
            skLineSegment(sketch, "E367", {"start": v(-36.68, 14.76) * mm, "end": v(-36.9, 14.74) * mm});
            skLineSegment(sketch, "E368", {"start": v(-36.9, 14.74) * mm, "end": v(-37.1, 14.72) * mm});
            skLineSegment(sketch, "E369", {"start": v(-37.1, 14.72) * mm, "end": v(-37.32, 14.7) * mm});
            skLineSegment(sketch, "E370", {"start": v(-37.32, 14.7) * mm, "end": v(-37.54, 14.67) * mm});
            skLineSegment(sketch, "E371", {"start": v(-37.54, 14.67) * mm, "end": v(-37.77, 14.64) * mm});
            skLineSegment(sketch, "E372", {"start": v(-37.77, 14.64) * mm, "end": v(-38, 14.6) * mm});
            skLineSegment(sketch, "E373", {"start": v(-38, 14.6) * mm, "end": v(-38.23, 14.57) * mm});
            skLineSegment(sketch, "E374", {"start": v(-38.23, 14.57) * mm, "end": v(-38.47, 14.52) * mm});
            skLineSegment(sketch, "E375", {"start": v(-38.47, 14.52) * mm, "end": v(-38.71, 14.48) * mm});
            skLineSegment(sketch, "E376", {"start": v(-38.71, 14.48) * mm, "end": v(-38.96, 14.43) * mm});
            skLineSegment(sketch, "E377", {"start": v(-38.96, 14.43) * mm, "end": v(-39.2, 14.38) * mm});
            skLineSegment(sketch, "E378", {"start": v(-39.2, 14.38) * mm, "end": v(-39.46, 14.32) * mm});
            skLineSegment(sketch, "E379", {"start": v(-39.46, 14.32) * mm, "end": v(-39.72, 14.27) * mm});
            skLineSegment(sketch, "E380", {"start": v(-39.72, 14.27) * mm, "end": v(-39.9, 14.17) * mm});
            skLineSegment(sketch, "E381", {"start": v(-39.9, 14.17) * mm, "end": v(-40.2, 13.27) * mm});
            skLineSegment(sketch, "E382", {"start": v(-40.2, 13.27) * mm, "end": v(-40.12, 13.1) * mm});
            skLineSegment(sketch, "E383", {"start": v(-40.12, 13.1) * mm, "end": v(-39.96, 12.89) * mm});
            skLineSegment(sketch, "E384", {"start": v(-39.96, 12.89) * mm, "end": v(-39.79, 12.69) * mm});
            skLineSegment(sketch, "E385", {"start": v(-39.79, 12.69) * mm, "end": v(-39.62, 12.5) * mm});
            skLineSegment(sketch, "E386", {"start": v(-39.62, 12.5) * mm, "end": v(-39.46, 12.3) * mm});
            skLineSegment(sketch, "E387", {"start": v(-39.46, 12.3) * mm, "end": v(-39.3, 12.12) * mm});
            skLineSegment(sketch, "E388", {"start": v(-39.3, 12.12) * mm, "end": v(-39.13, 11.94) * mm});
            skLineSegment(sketch, "E389", {"start": v(-39.13, 11.94) * mm, "end": v(-38.97, 11.77) * mm});
            skLineSegment(sketch, "E390", {"start": v(-38.97, 11.77) * mm, "end": v(-38.8, 11.6) * mm});
            skLineSegment(sketch, "E391", {"start": v(-38.8, 11.6) * mm, "end": v(-38.65, 11.44) * mm});
            skLineSegment(sketch, "E392", {"start": v(-38.65, 11.44) * mm, "end": v(-38.49, 11.28) * mm});
            skLineSegment(sketch, "E393", {"start": v(-38.49, 11.28) * mm, "end": v(-38.33, 11.13) * mm});
            skLineSegment(sketch, "E394", {"start": v(-38.33, 11.13) * mm, "end": v(-38.18, 10.98) * mm});
            skLineSegment(sketch, "E395", {"start": v(-38.18, 10.98) * mm, "end": v(-38.03, 10.84) * mm});
            skLineSegment(sketch, "E396", {"start": v(-38.03, 10.84) * mm, "end": v(-37.88, 10.7) * mm});
            skLineSegment(sketch, "E397", {"start": v(-37.88, 10.7) * mm, "end": v(-37.73, 10.57) * mm});
            skLineSegment(sketch, "E398", {"start": v(-37.73, 10.57) * mm, "end": v(-37.58, 10.45) * mm});
            skLineSegment(sketch, "E399", {"start": v(-37.58, 10.45) * mm, "end": v(-37.43, 10.32) * mm});
            skLineSegment(sketch, "E400", {"start": v(-37.43, 10.32) * mm, "end": v(-37.3, 10.2) * mm});
            skLineSegment(sketch, "E401", {"start": v(-37.3, 10.2) * mm, "end": v(-37.15, 10.1) * mm});
            skLineSegment(sketch, "E402", {"start": v(-37.15, 10.1) * mm, "end": v(-37.02, 9.99) * mm});
            skLineSegment(sketch, "E403", {"start": v(-37.02, 9.99) * mm, "end": v(-36.88, 9.88) * mm});
            skLineSegment(sketch, "E404", {"start": v(-36.88, 9.88) * mm, "end": v(-36.75, 9.78) * mm});
            skLineSegment(sketch, "E405", {"start": v(-36.75, 9.78) * mm, "end": v(-36.62, 9.7) * mm});
            skLineSegment(sketch, "E406", {"start": v(-36.62, 9.7) * mm, "end": v(-36.5, 9.6) * mm});
            skLineSegment(sketch, "E407", {"start": v(-36.5, 9.6) * mm, "end": v(-36.37, 9.51) * mm});
            skLineSegment(sketch, "E408", {"start": v(-36.37, 9.51) * mm, "end": v(-36.25, 9.43) * mm});
            skLineSegment(sketch, "E409", {"start": v(-36.25, 9.43) * mm, "end": v(-36.13, 9.35) * mm});
            skLineSegment(sketch, "E410", {"start": v(-36.13, 9.35) * mm, "end": v(-36.02, 9.28) * mm});
            skLineSegment(sketch, "E411", {"start": v(-36.02, 9.28) * mm, "end": v(-35.9, 9.2) * mm});
            skLineSegment(sketch, "E412", {"start": v(-35.9, 9.2) * mm, "end": v(-35.8, 9.14) * mm});
            skLineSegment(sketch, "E413", {"start": v(-35.8, 9.14) * mm, "end": v(-35.7, 9.08) * mm});
            skLineSegment(sketch, "E414", {"start": v(-35.7, 9.08) * mm, "end": v(-35.59, 9.02) * mm});
            skLineSegment(sketch, "E415", {"start": v(-4.18, 36.7) * mm, "end": v(-4.23, 36.82) * mm});
            skLineSegment(sketch, "E416", {"start": v(0, -2.65) * mm, "end": v(0, 2.65) * mm});
            skCircle(sketch, "E417", {"center": v(0, 0) * mm, "radius": 6 * mm});
            skCircle(sketch, "E418", {"center": v(0, 0) * mm, "radius": 4.1 * mm});
            skArc(sketch, "E419", {"start": v(0.4, 9.03) * mm, "mid": v(-5.94, 6.8) * mm, "end": v(-9, 0.83) * mm});
            skPoint(sketch, "E420.orphan", {"position": v(0.6, 5.97) * mm});
            skPoint(sketch, "E421.orphan", {"position": v(-6, 0.21) * mm});
            skLineSegment(sketch, "E422", {"start": v(-4.1, 36.49) * mm, "end": v(5.77, 1.63) * mm});
            skLineSegment(sketch, "E423", {"start": v(-35.59, 9.02) * mm, "end": v(-1.83, -5.75) * mm});
            skLineSegment(sketch, "E424", {"start": v(0.4, 9.03) * mm, "end": v(-5.04, 28.27) * mm});
            skLineSegment(sketch, "E425", {"start": v(-9, 0.83) * mm, "end": v(-27.32, 8.85) * mm});
            skArc(sketch, "E426", {"start": v(-5.04, 28.27) * mm, "mid": v(-21.07, 24.17) * mm, "end": v(-27.32, 8.85) * mm});
            skLineSegment(sketch, "E427", {"start": v(-4.18, 36.7) * mm, "end": v(-4.14, 36.6) * mm});
            skSolve(sketch);
        }
        {
            var Q0;
            Q0=makeQuery(id+"F0.imprint","IMPRINT",FACE,{"disambiguationData":[TD([[makeQuery(id+"F0.imprint","IMPRINT",EDGE,{"derivedFrom":sQuery(id+"F0.wireOp",EDGE,"E418")}),-1.0]])]});
            extrude(context, id + "F1", {"entities" : qUnion([Q0]), "depth" : 10 * mm, "offsetDistance" : 25 * mm, "hasSecondDirection" : true, "secondDirectionOppositeDirection" : true, "secondDirectionDepth" : 3 * mm});
        }
        {
            var Q0;
            {var subQ0=sQuery(id+"F0.wireOp",EDGE,"0ef48464-72c9-4203-a87e-13357dbbfc55");Q0=makeQuery(id+"F0.imprint","IMPRINT",FACE,{"disambiguationData":[TD([[makeQuery(id+"F0.imprint","IMPRINT",EDGE,{"derivedFrom":subQ0}),1.0]])]});}
            var Q1;
            Q1=makeQuery(id+"F0.imprint","IMPRINT",FACE,{"disambiguationData":[TD([[makeQuery(id+"F0.imprint","IMPRINT",EDGE,{"derivedFrom":sQuery(id+"F0.wireOp",EDGE,"E418")}),-1.0]])]});
            extrude(context, id + "F2", {"entities" : qUnion([Q0, Q1]), "operationType" : NewBodyOperationType.ADD, "oppositeDirection" : true, "depth" : 3 * mm, "offsetDistance" : 25 * mm});
        }
        {
            var Q0;
            Q0=makeQuery(id+"F0.imprint","IMPRINT",FACE,{"disambiguationData":[TD([[makeQuery(id+"F0.imprint","IMPRINT",EDGE,{"derivedFrom":sQuery(id+"F0.wireOp",EDGE,"E0")}),1.0]])]});
            extrude(context, id + "F3", {"entities" : qUnion([Q0]), "operationType" : NewBodyOperationType.ADD, "oppositeDirection" : true, "depth" : 3 * mm, "offsetDistance" : 25 * mm});
        }
        {
            var Q0;
            {var subQ0=sQuery(id+"F0.wireOp",EDGE,"E417");Q0=makeQuery(id+"F3.boolean.opBoolean","MERGE",FACE,{"derivedFrom":[makeQuery(id+"F2.opExtrude","CAP_FACE",FACE,{"disambiguationData":[OSD([subQ0,sQuery(id+"F0.wireOp",EDGE,"E418")])],"isStart":false}),makeQuery(id+"F3.opExtrude","CAP_FACE",FACE,{"disambiguationData":[OSD([sQuery(id+"F0.wireOp",EDGE,"E0"),sQuery(id+"F0.wireOp",EDGE,"E415"),sQuery(id+"F0.wireOp",EDGE,"E1"),sQuery(id+"F0.wireOp",EDGE,"E2"),sQuery(id+"F0.wireOp",EDGE,"E3"),sQuery(id+"F0.wireOp",EDGE,"E4"),sQuery(id+"F0.wireOp",EDGE,"E5"),sQuery(id+"F0.wireOp",EDGE,"E6"),sQuery(id+"F0.wireOp",EDGE,"E7"),sQuery(id+"F0.wireOp",EDGE,"E8"),sQuery(id+"F0.wireOp",EDGE,"E9"),sQuery(id+"F0.wireOp",EDGE,"E10"),sQuery(id+"F0.wireOp",EDGE,"E11"),sQuery(id+"F0.wireOp",EDGE,"E12"),sQuery(id+"F0.wireOp",EDGE,"E13"),sQuery(id+"F0.wireOp",EDGE,"E14"),sQuery(id+"F0.wireOp",EDGE,"E15"),sQuery(id+"F0.wireOp",EDGE,"E16"),sQuery(id+"F0.wireOp",EDGE,"E17"),sQuery(id+"F0.wireOp",EDGE,"E18"),sQuery(id+"F0.wireOp",EDGE,"E19"),sQuery(id+"F0.wireOp",EDGE,"E20"),sQuery(id+"F0.wireOp",EDGE,"E21"),sQuery(id+"F0.wireOp",EDGE,"E22"),sQuery(id+"F0.wireOp",EDGE,"E23"),sQuery(id+"F0.wireOp",EDGE,"E24"),sQuery(id+"F0.wireOp",EDGE,"E25"),sQuery(id+"F0.wireOp",EDGE,"E26"),sQuery(id+"F0.wireOp",EDGE,"E27"),sQuery(id+"F0.wireOp",EDGE,"E28"),sQuery(id+"F0.wireOp",EDGE,"E29"),sQuery(id+"F0.wireOp",EDGE,"E30"),sQuery(id+"F0.wireOp",EDGE,"E31"),sQuery(id+"F0.wireOp",EDGE,"E32"),sQuery(id+"F0.wireOp",EDGE,"E33"),sQuery(id+"F0.wireOp",EDGE,"E34"),sQuery(id+"F0.wireOp",EDGE,"E35"),sQuery(id+"F0.wireOp",EDGE,"E36"),sQuery(id+"F0.wireOp",EDGE,"E37"),sQuery(id+"F0.wireOp",EDGE,"E38"),sQuery(id+"F0.wireOp",EDGE,"E39"),sQuery(id+"F0.wireOp",EDGE,"E40"),sQuery(id+"F0.wireOp",EDGE,"E41"),sQuery(id+"F0.wireOp",EDGE,"E42"),sQuery(id+"F0.wireOp",EDGE,"E43"),sQuery(id+"F0.wireOp",EDGE,"E44"),sQuery(id+"F0.wireOp",EDGE,"E45"),sQuery(id+"F0.wireOp",EDGE,"E46"),sQuery(id+"F0.wireOp",EDGE,"E47"),sQuery(id+"F0.wireOp",EDGE,"E48"),sQuery(id+"F0.wireOp",EDGE,"E49"),sQuery(id+"F0.wireOp",EDGE,"E50"),sQuery(id+"F0.wireOp",EDGE,"E51"),sQuery(id+"F0.wireOp",EDGE,"E52"),sQuery(id+"F0.wireOp",EDGE,"E53"),sQuery(id+"F0.wireOp",EDGE,"E54"),sQuery(id+"F0.wireOp",EDGE,"E55"),sQuery(id+"F0.wireOp",EDGE,"E56"),sQuery(id+"F0.wireOp",EDGE,"E57"),sQuery(id+"F0.wireOp",EDGE,"E58"),sQuery(id+"F0.wireOp",EDGE,"E59"),sQuery(id+"F0.wireOp",EDGE,"E60"),sQuery(id+"F0.wireOp",EDGE,"E61"),sQuery(id+"F0.wireOp",EDGE,"E62"),sQuery(id+"F0.wireOp",EDGE,"E63"),sQuery(id+"F0.wireOp",EDGE,"E64"),sQuery(id+"F0.wireOp",EDGE,"E65"),sQuery(id+"F0.wireOp",EDGE,"E66"),sQuery(id+"F0.wireOp",EDGE,"E67"),sQuery(id+"F0.wireOp",EDGE,"E68"),sQuery(id+"F0.wireOp",EDGE,"E69"),sQuery(id+"F0.wireOp",EDGE,"E70"),sQuery(id+"F0.wireOp",EDGE,"E71"),sQuery(id+"F0.wireOp",EDGE,"E72"),sQuery(id+"F0.wireOp",EDGE,"E73"),sQuery(id+"F0.wireOp",EDGE,"E74"),sQuery(id+"F0.wireOp",EDGE,"E75"),sQuery(id+"F0.wireOp",EDGE,"E76"),sQuery(id+"F0.wireOp",EDGE,"E77"),sQuery(id+"F0.wireOp",EDGE,"E78"),sQuery(id+"F0.wireOp",EDGE,"E79"),sQuery(id+"F0.wireOp",EDGE,"E80"),sQuery(id+"F0.wireOp",EDGE,"E81"),sQuery(id+"F0.wireOp",EDGE,"E82"),sQuery(id+"F0.wireOp",EDGE,"E83"),sQuery(id+"F0.wireOp",EDGE,"E84"),sQuery(id+"F0.wireOp",EDGE,"E85"),sQuery(id+"F0.wireOp",EDGE,"E86"),sQuery(id+"F0.wireOp",EDGE,"E87"),sQuery(id+"F0.wireOp",EDGE,"E88"),sQuery(id+"F0.wireOp",EDGE,"E89"),sQuery(id+"F0.wireOp",EDGE,"E90"),sQuery(id+"F0.wireOp",EDGE,"E91"),sQuery(id+"F0.wireOp",EDGE,"E92"),sQuery(id+"F0.wireOp",EDGE,"E93"),sQuery(id+"F0.wireOp",EDGE,"E94"),sQuery(id+"F0.wireOp",EDGE,"E95"),sQuery(id+"F0.wireOp",EDGE,"E96"),sQuery(id+"F0.wireOp",EDGE,"E97"),sQuery(id+"F0.wireOp",EDGE,"E98"),sQuery(id+"F0.wireOp",EDGE,"E99"),sQuery(id+"F0.wireOp",EDGE,"E100"),sQuery(id+"F0.wireOp",EDGE,"E101"),sQuery(id+"F0.wireOp",EDGE,"E102"),sQuery(id+"F0.wireOp",EDGE,"E103"),sQuery(id+"F0.wireOp",EDGE,"E104"),sQuery(id+"F0.wireOp",EDGE,"E105"),sQuery(id+"F0.wireOp",EDGE,"E106"),sQuery(id+"F0.wireOp",EDGE,"E107"),sQuery(id+"F0.wireOp",EDGE,"E108"),sQuery(id+"F0.wireOp",EDGE,"E109"),sQuery(id+"F0.wireOp",EDGE,"E110"),sQuery(id+"F0.wireOp",EDGE,"E111"),sQuery(id+"F0.wireOp",EDGE,"E112"),sQuery(id+"F0.wireOp",EDGE,"E113"),sQuery(id+"F0.wireOp",EDGE,"E114"),sQuery(id+"F0.wireOp",EDGE,"E115"),sQuery(id+"F0.wireOp",EDGE,"E116"),sQuery(id+"F0.wireOp",EDGE,"E117"),sQuery(id+"F0.wireOp",EDGE,"E118"),sQuery(id+"F0.wireOp",EDGE,"E119"),sQuery(id+"F0.wireOp",EDGE,"E120"),sQuery(id+"F0.wireOp",EDGE,"E121"),sQuery(id+"F0.wireOp",EDGE,"E122"),sQuery(id+"F0.wireOp",EDGE,"E123"),sQuery(id+"F0.wireOp",EDGE,"E124"),sQuery(id+"F0.wireOp",EDGE,"E125"),sQuery(id+"F0.wireOp",EDGE,"E126"),sQuery(id+"F0.wireOp",EDGE,"E127"),sQuery(id+"F0.wireOp",EDGE,"E128"),sQuery(id+"F0.wireOp",EDGE,"E129"),sQuery(id+"F0.wireOp",EDGE,"E130"),sQuery(id+"F0.wireOp",EDGE,"E131"),sQuery(id+"F0.wireOp",EDGE,"E132"),sQuery(id+"F0.wireOp",EDGE,"E133"),sQuery(id+"F0.wireOp",EDGE,"E134"),sQuery(id+"F0.wireOp",EDGE,"E135"),sQuery(id+"F0.wireOp",EDGE,"E136"),sQuery(id+"F0.wireOp",EDGE,"E137"),sQuery(id+"F0.wireOp",EDGE,"E138"),sQuery(id+"F0.wireOp",EDGE,"E139"),sQuery(id+"F0.wireOp",EDGE,"E140"),sQuery(id+"F0.wireOp",EDGE,"E141"),sQuery(id+"F0.wireOp",EDGE,"E142"),sQuery(id+"F0.wireOp",EDGE,"E143"),sQuery(id+"F0.wireOp",EDGE,"E144"),sQuery(id+"F0.wireOp",EDGE,"E145"),sQuery(id+"F0.wireOp",EDGE,"E146"),sQuery(id+"F0.wireOp",EDGE,"E147"),sQuery(id+"F0.wireOp",EDGE,"E148"),sQuery(id+"F0.wireOp",EDGE,"E149"),sQuery(id+"F0.wireOp",EDGE,"E150"),sQuery(id+"F0.wireOp",EDGE,"E151"),sQuery(id+"F0.wireOp",EDGE,"E152"),sQuery(id+"F0.wireOp",EDGE,"E153"),sQuery(id+"F0.wireOp",EDGE,"E154"),sQuery(id+"F0.wireOp",EDGE,"E155"),sQuery(id+"F0.wireOp",EDGE,"E156"),sQuery(id+"F0.wireOp",EDGE,"E157"),sQuery(id+"F0.wireOp",EDGE,"E158"),sQuery(id+"F0.wireOp",EDGE,"E159"),sQuery(id+"F0.wireOp",EDGE,"E160"),sQuery(id+"F0.wireOp",EDGE,"E161"),sQuery(id+"F0.wireOp",EDGE,"E162"),sQuery(id+"F0.wireOp",EDGE,"E163"),sQuery(id+"F0.wireOp",EDGE,"E164"),sQuery(id+"F0.wireOp",EDGE,"E165"),sQuery(id+"F0.wireOp",EDGE,"E166"),sQuery(id+"F0.wireOp",EDGE,"E167"),sQuery(id+"F0.wireOp",EDGE,"E168"),sQuery(id+"F0.wireOp",EDGE,"E169"),sQuery(id+"F0.wireOp",EDGE,"E170"),sQuery(id+"F0.wireOp",EDGE,"E171"),sQuery(id+"F0.wireOp",EDGE,"E172"),sQuery(id+"F0.wireOp",EDGE,"E173"),sQuery(id+"F0.wireOp",EDGE,"E174"),sQuery(id+"F0.wireOp",EDGE,"E175"),sQuery(id+"F0.wireOp",EDGE,"E176"),sQuery(id+"F0.wireOp",EDGE,"E177"),sQuery(id+"F0.wireOp",EDGE,"E178"),sQuery(id+"F0.wireOp",EDGE,"E179"),sQuery(id+"F0.wireOp",EDGE,"E180"),sQuery(id+"F0.wireOp",EDGE,"E181"),sQuery(id+"F0.wireOp",EDGE,"E182"),sQuery(id+"F0.wireOp",EDGE,"E183"),sQuery(id+"F0.wireOp",EDGE,"E184"),sQuery(id+"F0.wireOp",EDGE,"E185"),sQuery(id+"F0.wireOp",EDGE,"E186"),sQuery(id+"F0.wireOp",EDGE,"E187"),sQuery(id+"F0.wireOp",EDGE,"E188"),sQuery(id+"F0.wireOp",EDGE,"E189"),sQuery(id+"F0.wireOp",EDGE,"E190"),sQuery(id+"F0.wireOp",EDGE,"E191"),sQuery(id+"F0.wireOp",EDGE,"E192"),sQuery(id+"F0.wireOp",EDGE,"E193"),sQuery(id+"F0.wireOp",EDGE,"E194"),sQuery(id+"F0.wireOp",EDGE,"E195"),sQuery(id+"F0.wireOp",EDGE,"E196"),sQuery(id+"F0.wireOp",EDGE,"E197"),sQuery(id+"F0.wireOp",EDGE,"E198"),sQuery(id+"F0.wireOp",EDGE,"E199"),sQuery(id+"F0.wireOp",EDGE,"E200"),sQuery(id+"F0.wireOp",EDGE,"E201"),sQuery(id+"F0.wireOp",EDGE,"E202"),sQuery(id+"F0.wireOp",EDGE,"E203"),sQuery(id+"F0.wireOp",EDGE,"E204"),sQuery(id+"F0.wireOp",EDGE,"E205"),sQuery(id+"F0.wireOp",EDGE,"E206"),sQuery(id+"F0.wireOp",EDGE,"E207"),sQuery(id+"F0.wireOp",EDGE,"E208"),sQuery(id+"F0.wireOp",EDGE,"E209"),sQuery(id+"F0.wireOp",EDGE,"E210"),sQuery(id+"F0.wireOp",EDGE,"E211"),sQuery(id+"F0.wireOp",EDGE,"E212"),sQuery(id+"F0.wireOp",EDGE,"E213"),sQuery(id+"F0.wireOp",EDGE,"E214"),sQuery(id+"F0.wireOp",EDGE,"E215"),sQuery(id+"F0.wireOp",EDGE,"E216"),sQuery(id+"F0.wireOp",EDGE,"E217"),sQuery(id+"F0.wireOp",EDGE,"E218"),sQuery(id+"F0.wireOp",EDGE,"E219"),sQuery(id+"F0.wireOp",EDGE,"E220"),sQuery(id+"F0.wireOp",EDGE,"E221"),sQuery(id+"F0.wireOp",EDGE,"E222"),sQuery(id+"F0.wireOp",EDGE,"E223"),sQuery(id+"F0.wireOp",EDGE,"E224"),sQuery(id+"F0.wireOp",EDGE,"E225"),sQuery(id+"F0.wireOp",EDGE,"E226"),sQuery(id+"F0.wireOp",EDGE,"E227"),sQuery(id+"F0.wireOp",EDGE,"E228"),sQuery(id+"F0.wireOp",EDGE,"E229"),sQuery(id+"F0.wireOp",EDGE,"E230"),sQuery(id+"F0.wireOp",EDGE,"E231"),sQuery(id+"F0.wireOp",EDGE,"E232"),sQuery(id+"F0.wireOp",EDGE,"E233"),sQuery(id+"F0.wireOp",EDGE,"E234"),sQuery(id+"F0.wireOp",EDGE,"E235"),sQuery(id+"F0.wireOp",EDGE,"E236"),sQuery(id+"F0.wireOp",EDGE,"E237"),sQuery(id+"F0.wireOp",EDGE,"E238"),sQuery(id+"F0.wireOp",EDGE,"E239"),sQuery(id+"F0.wireOp",EDGE,"E240"),sQuery(id+"F0.wireOp",EDGE,"E241"),sQuery(id+"F0.wireOp",EDGE,"E242"),sQuery(id+"F0.wireOp",EDGE,"E243"),sQuery(id+"F0.wireOp",EDGE,"E244"),sQuery(id+"F0.wireOp",EDGE,"E245"),sQuery(id+"F0.wireOp",EDGE,"E246"),sQuery(id+"F0.wireOp",EDGE,"E247"),sQuery(id+"F0.wireOp",EDGE,"E248"),sQuery(id+"F0.wireOp",EDGE,"E249"),sQuery(id+"F0.wireOp",EDGE,"E250"),sQuery(id+"F0.wireOp",EDGE,"E251"),sQuery(id+"F0.wireOp",EDGE,"E252"),sQuery(id+"F0.wireOp",EDGE,"E253"),sQuery(id+"F0.wireOp",EDGE,"E254"),sQuery(id+"F0.wireOp",EDGE,"E255"),sQuery(id+"F0.wireOp",EDGE,"E256"),sQuery(id+"F0.wireOp",EDGE,"E257"),sQuery(id+"F0.wireOp",EDGE,"E258"),sQuery(id+"F0.wireOp",EDGE,"E259"),sQuery(id+"F0.wireOp",EDGE,"E260"),sQuery(id+"F0.wireOp",EDGE,"E261"),sQuery(id+"F0.wireOp",EDGE,"E262"),sQuery(id+"F0.wireOp",EDGE,"E263"),sQuery(id+"F0.wireOp",EDGE,"E264"),sQuery(id+"F0.wireOp",EDGE,"E265"),sQuery(id+"F0.wireOp",EDGE,"E266"),sQuery(id+"F0.wireOp",EDGE,"E267"),sQuery(id+"F0.wireOp",EDGE,"E268"),sQuery(id+"F0.wireOp",EDGE,"E269"),sQuery(id+"F0.wireOp",EDGE,"E270"),sQuery(id+"F0.wireOp",EDGE,"E271"),sQuery(id+"F0.wireOp",EDGE,"E272"),sQuery(id+"F0.wireOp",EDGE,"E273"),sQuery(id+"F0.wireOp",EDGE,"E274"),sQuery(id+"F0.wireOp",EDGE,"E275"),sQuery(id+"F0.wireOp",EDGE,"E276"),sQuery(id+"F0.wireOp",EDGE,"E277"),sQuery(id+"F0.wireOp",EDGE,"E278"),sQuery(id+"F0.wireOp",EDGE,"E279"),sQuery(id+"F0.wireOp",EDGE,"E280"),sQuery(id+"F0.wireOp",EDGE,"E281"),sQuery(id+"F0.wireOp",EDGE,"E282"),sQuery(id+"F0.wireOp",EDGE,"E283"),sQuery(id+"F0.wireOp",EDGE,"E284"),sQuery(id+"F0.wireOp",EDGE,"E285"),sQuery(id+"F0.wireOp",EDGE,"E286"),sQuery(id+"F0.wireOp",EDGE,"E287"),sQuery(id+"F0.wireOp",EDGE,"E288"),sQuery(id+"F0.wireOp",EDGE,"E289"),sQuery(id+"F0.wireOp",EDGE,"E290"),sQuery(id+"F0.wireOp",EDGE,"E291"),sQuery(id+"F0.wireOp",EDGE,"E292"),sQuery(id+"F0.wireOp",EDGE,"E293"),sQuery(id+"F0.wireOp",EDGE,"E294"),sQuery(id+"F0.wireOp",EDGE,"E295"),sQuery(id+"F0.wireOp",EDGE,"E296"),sQuery(id+"F0.wireOp",EDGE,"E297"),sQuery(id+"F0.wireOp",EDGE,"E298"),sQuery(id+"F0.wireOp",EDGE,"E299"),sQuery(id+"F0.wireOp",EDGE,"E300"),sQuery(id+"F0.wireOp",EDGE,"E301"),sQuery(id+"F0.wireOp",EDGE,"E302"),sQuery(id+"F0.wireOp",EDGE,"E303"),sQuery(id+"F0.wireOp",EDGE,"E304"),sQuery(id+"F0.wireOp",EDGE,"E305"),sQuery(id+"F0.wireOp",EDGE,"E306"),sQuery(id+"F0.wireOp",EDGE,"E307"),sQuery(id+"F0.wireOp",EDGE,"E308"),sQuery(id+"F0.wireOp",EDGE,"E309"),sQuery(id+"F0.wireOp",EDGE,"E310"),sQuery(id+"F0.wireOp",EDGE,"E311"),sQuery(id+"F0.wireOp",EDGE,"E312"),sQuery(id+"F0.wireOp",EDGE,"E313"),sQuery(id+"F0.wireOp",EDGE,"E314"),sQuery(id+"F0.wireOp",EDGE,"E315"),sQuery(id+"F0.wireOp",EDGE,"E316"),sQuery(id+"F0.wireOp",EDGE,"E317"),sQuery(id+"F0.wireOp",EDGE,"E318"),sQuery(id+"F0.wireOp",EDGE,"E319"),sQuery(id+"F0.wireOp",EDGE,"E320"),sQuery(id+"F0.wireOp",EDGE,"E321"),sQuery(id+"F0.wireOp",EDGE,"E322"),sQuery(id+"F0.wireOp",EDGE,"E323"),sQuery(id+"F0.wireOp",EDGE,"E324"),sQuery(id+"F0.wireOp",EDGE,"E325"),sQuery(id+"F0.wireOp",EDGE,"E326"),sQuery(id+"F0.wireOp",EDGE,"E327"),sQuery(id+"F0.wireOp",EDGE,"E328"),sQuery(id+"F0.wireOp",EDGE,"E329"),sQuery(id+"F0.wireOp",EDGE,"E330"),sQuery(id+"F0.wireOp",EDGE,"E331"),sQuery(id+"F0.wireOp",EDGE,"E332"),sQuery(id+"F0.wireOp",EDGE,"E333"),sQuery(id+"F0.wireOp",EDGE,"E334"),sQuery(id+"F0.wireOp",EDGE,"E335"),sQuery(id+"F0.wireOp",EDGE,"E336"),sQuery(id+"F0.wireOp",EDGE,"E337"),sQuery(id+"F0.wireOp",EDGE,"E338"),sQuery(id+"F0.wireOp",EDGE,"E339"),sQuery(id+"F0.wireOp",EDGE,"E340"),sQuery(id+"F0.wireOp",EDGE,"E341"),sQuery(id+"F0.wireOp",EDGE,"E342"),sQuery(id+"F0.wireOp",EDGE,"E343"),sQuery(id+"F0.wireOp",EDGE,"E344"),sQuery(id+"F0.wireOp",EDGE,"E345"),sQuery(id+"F0.wireOp",EDGE,"E346"),sQuery(id+"F0.wireOp",EDGE,"E347"),sQuery(id+"F0.wireOp",EDGE,"E348"),sQuery(id+"F0.wireOp",EDGE,"E349"),sQuery(id+"F0.wireOp",EDGE,"E350"),sQuery(id+"F0.wireOp",EDGE,"E351"),sQuery(id+"F0.wireOp",EDGE,"E352"),sQuery(id+"F0.wireOp",EDGE,"E353"),sQuery(id+"F0.wireOp",EDGE,"E354"),sQuery(id+"F0.wireOp",EDGE,"E355"),sQuery(id+"F0.wireOp",EDGE,"E356"),sQuery(id+"F0.wireOp",EDGE,"E357"),sQuery(id+"F0.wireOp",EDGE,"E358"),sQuery(id+"F0.wireOp",EDGE,"E359"),sQuery(id+"F0.wireOp",EDGE,"E360"),sQuery(id+"F0.wireOp",EDGE,"E361"),sQuery(id+"F0.wireOp",EDGE,"E362"),sQuery(id+"F0.wireOp",EDGE,"E363"),sQuery(id+"F0.wireOp",EDGE,"E364"),sQuery(id+"F0.wireOp",EDGE,"E365"),sQuery(id+"F0.wireOp",EDGE,"E366"),sQuery(id+"F0.wireOp",EDGE,"E367"),sQuery(id+"F0.wireOp",EDGE,"E368"),sQuery(id+"F0.wireOp",EDGE,"E369"),sQuery(id+"F0.wireOp",EDGE,"E370"),sQuery(id+"F0.wireOp",EDGE,"E371"),sQuery(id+"F0.wireOp",EDGE,"E372"),sQuery(id+"F0.wireOp",EDGE,"E373"),sQuery(id+"F0.wireOp",EDGE,"E374"),sQuery(id+"F0.wireOp",EDGE,"E375"),sQuery(id+"F0.wireOp",EDGE,"E376"),sQuery(id+"F0.wireOp",EDGE,"E377"),sQuery(id+"F0.wireOp",EDGE,"E378"),sQuery(id+"F0.wireOp",EDGE,"E379"),sQuery(id+"F0.wireOp",EDGE,"E380"),sQuery(id+"F0.wireOp",EDGE,"E381"),sQuery(id+"F0.wireOp",EDGE,"E382"),sQuery(id+"F0.wireOp",EDGE,"E383"),sQuery(id+"F0.wireOp",EDGE,"E384"),sQuery(id+"F0.wireOp",EDGE,"E385"),sQuery(id+"F0.wireOp",EDGE,"E386"),sQuery(id+"F0.wireOp",EDGE,"E387"),sQuery(id+"F0.wireOp",EDGE,"E388"),sQuery(id+"F0.wireOp",EDGE,"E389"),sQuery(id+"F0.wireOp",EDGE,"E390"),sQuery(id+"F0.wireOp",EDGE,"E391"),sQuery(id+"F0.wireOp",EDGE,"E392"),sQuery(id+"F0.wireOp",EDGE,"E393"),sQuery(id+"F0.wireOp",EDGE,"E394"),sQuery(id+"F0.wireOp",EDGE,"E395"),sQuery(id+"F0.wireOp",EDGE,"E396"),sQuery(id+"F0.wireOp",EDGE,"E397"),sQuery(id+"F0.wireOp",EDGE,"E398"),sQuery(id+"F0.wireOp",EDGE,"E399"),sQuery(id+"F0.wireOp",EDGE,"E400"),sQuery(id+"F0.wireOp",EDGE,"E401"),sQuery(id+"F0.wireOp",EDGE,"E402"),sQuery(id+"F0.wireOp",EDGE,"E403"),sQuery(id+"F0.wireOp",EDGE,"E404"),sQuery(id+"F0.wireOp",EDGE,"E405"),sQuery(id+"F0.wireOp",EDGE,"E406"),sQuery(id+"F0.wireOp",EDGE,"E407"),sQuery(id+"F0.wireOp",EDGE,"E408"),sQuery(id+"F0.wireOp",EDGE,"E409"),sQuery(id+"F0.wireOp",EDGE,"E410"),sQuery(id+"F0.wireOp",EDGE,"E411"),sQuery(id+"F0.wireOp",EDGE,"E412"),sQuery(id+"F0.wireOp",EDGE,"E413"),sQuery(id+"F0.wireOp",EDGE,"E414"),subQ0,sQuery(id+"F0.wireOp",EDGE,"E419"),sQuery(id+"F0.wireOp",EDGE,"E422"),sQuery(id+"F0.wireOp",EDGE,"E423"),sQuery(id+"F0.wireOp",EDGE,"E424"),sQuery(id+"F0.wireOp",EDGE,"E425"),sQuery(id+"F0.wireOp",EDGE,"E426"),sQuery(id+"F0.wireOp",EDGE,"E427")])],"isStart":false})]});}
            var Q1;
            Q1=makeQuery(id+"F3.opExtrude","CAP_FACE",FACE,{"disambiguationData":[OSD([sQuery(id+"F0.wireOp",EDGE,"E0"),sQuery(id+"F0.wireOp",EDGE,"E415"),sQuery(id+"F0.wireOp",EDGE,"E1"),sQuery(id+"F0.wireOp",EDGE,"E2"),sQuery(id+"F0.wireOp",EDGE,"E3"),sQuery(id+"F0.wireOp",EDGE,"E4"),sQuery(id+"F0.wireOp",EDGE,"E5"),sQuery(id+"F0.wireOp",EDGE,"E6"),sQuery(id+"F0.wireOp",EDGE,"E7"),sQuery(id+"F0.wireOp",EDGE,"E8"),sQuery(id+"F0.wireOp",EDGE,"E9"),sQuery(id+"F0.wireOp",EDGE,"E10"),sQuery(id+"F0.wireOp",EDGE,"E11"),sQuery(id+"F0.wireOp",EDGE,"E12"),sQuery(id+"F0.wireOp",EDGE,"E13"),sQuery(id+"F0.wireOp",EDGE,"E14"),sQuery(id+"F0.wireOp",EDGE,"E15"),sQuery(id+"F0.wireOp",EDGE,"E16"),sQuery(id+"F0.wireOp",EDGE,"E17"),sQuery(id+"F0.wireOp",EDGE,"E18"),sQuery(id+"F0.wireOp",EDGE,"E19"),sQuery(id+"F0.wireOp",EDGE,"E20"),sQuery(id+"F0.wireOp",EDGE,"E21"),sQuery(id+"F0.wireOp",EDGE,"E22"),sQuery(id+"F0.wireOp",EDGE,"E23"),sQuery(id+"F0.wireOp",EDGE,"E24"),sQuery(id+"F0.wireOp",EDGE,"E25"),sQuery(id+"F0.wireOp",EDGE,"E26"),sQuery(id+"F0.wireOp",EDGE,"E27"),sQuery(id+"F0.wireOp",EDGE,"E28"),sQuery(id+"F0.wireOp",EDGE,"E29"),sQuery(id+"F0.wireOp",EDGE,"E30"),sQuery(id+"F0.wireOp",EDGE,"E31"),sQuery(id+"F0.wireOp",EDGE,"E32"),sQuery(id+"F0.wireOp",EDGE,"E33"),sQuery(id+"F0.wireOp",EDGE,"E34"),sQuery(id+"F0.wireOp",EDGE,"E35"),sQuery(id+"F0.wireOp",EDGE,"E36"),sQuery(id+"F0.wireOp",EDGE,"E37"),sQuery(id+"F0.wireOp",EDGE,"E38"),sQuery(id+"F0.wireOp",EDGE,"E39"),sQuery(id+"F0.wireOp",EDGE,"E40"),sQuery(id+"F0.wireOp",EDGE,"E41"),sQuery(id+"F0.wireOp",EDGE,"E42"),sQuery(id+"F0.wireOp",EDGE,"E43"),sQuery(id+"F0.wireOp",EDGE,"E44"),sQuery(id+"F0.wireOp",EDGE,"E45"),sQuery(id+"F0.wireOp",EDGE,"E46"),sQuery(id+"F0.wireOp",EDGE,"E47"),sQuery(id+"F0.wireOp",EDGE,"E48"),sQuery(id+"F0.wireOp",EDGE,"E49"),sQuery(id+"F0.wireOp",EDGE,"E50"),sQuery(id+"F0.wireOp",EDGE,"E51"),sQuery(id+"F0.wireOp",EDGE,"E52"),sQuery(id+"F0.wireOp",EDGE,"E53"),sQuery(id+"F0.wireOp",EDGE,"E54"),sQuery(id+"F0.wireOp",EDGE,"E55"),sQuery(id+"F0.wireOp",EDGE,"E56"),sQuery(id+"F0.wireOp",EDGE,"E57"),sQuery(id+"F0.wireOp",EDGE,"E58"),sQuery(id+"F0.wireOp",EDGE,"E59"),sQuery(id+"F0.wireOp",EDGE,"E60"),sQuery(id+"F0.wireOp",EDGE,"E61"),sQuery(id+"F0.wireOp",EDGE,"E62"),sQuery(id+"F0.wireOp",EDGE,"E63"),sQuery(id+"F0.wireOp",EDGE,"E64"),sQuery(id+"F0.wireOp",EDGE,"E65"),sQuery(id+"F0.wireOp",EDGE,"E66"),sQuery(id+"F0.wireOp",EDGE,"E67"),sQuery(id+"F0.wireOp",EDGE,"E68"),sQuery(id+"F0.wireOp",EDGE,"E69"),sQuery(id+"F0.wireOp",EDGE,"E70"),sQuery(id+"F0.wireOp",EDGE,"E71"),sQuery(id+"F0.wireOp",EDGE,"E72"),sQuery(id+"F0.wireOp",EDGE,"E73"),sQuery(id+"F0.wireOp",EDGE,"E74"),sQuery(id+"F0.wireOp",EDGE,"E75"),sQuery(id+"F0.wireOp",EDGE,"E76"),sQuery(id+"F0.wireOp",EDGE,"E77"),sQuery(id+"F0.wireOp",EDGE,"E78"),sQuery(id+"F0.wireOp",EDGE,"E79"),sQuery(id+"F0.wireOp",EDGE,"E80"),sQuery(id+"F0.wireOp",EDGE,"E81"),sQuery(id+"F0.wireOp",EDGE,"E82"),sQuery(id+"F0.wireOp",EDGE,"E83"),sQuery(id+"F0.wireOp",EDGE,"E84"),sQuery(id+"F0.wireOp",EDGE,"E85"),sQuery(id+"F0.wireOp",EDGE,"E86"),sQuery(id+"F0.wireOp",EDGE,"E87"),sQuery(id+"F0.wireOp",EDGE,"E88"),sQuery(id+"F0.wireOp",EDGE,"E89"),sQuery(id+"F0.wireOp",EDGE,"E90"),sQuery(id+"F0.wireOp",EDGE,"E91"),sQuery(id+"F0.wireOp",EDGE,"E92"),sQuery(id+"F0.wireOp",EDGE,"E93"),sQuery(id+"F0.wireOp",EDGE,"E94"),sQuery(id+"F0.wireOp",EDGE,"E95"),sQuery(id+"F0.wireOp",EDGE,"E96"),sQuery(id+"F0.wireOp",EDGE,"E97"),sQuery(id+"F0.wireOp",EDGE,"E98"),sQuery(id+"F0.wireOp",EDGE,"E99"),sQuery(id+"F0.wireOp",EDGE,"E100"),sQuery(id+"F0.wireOp",EDGE,"E101"),sQuery(id+"F0.wireOp",EDGE,"E102"),sQuery(id+"F0.wireOp",EDGE,"E103"),sQuery(id+"F0.wireOp",EDGE,"E104"),sQuery(id+"F0.wireOp",EDGE,"E105"),sQuery(id+"F0.wireOp",EDGE,"E106"),sQuery(id+"F0.wireOp",EDGE,"E107"),sQuery(id+"F0.wireOp",EDGE,"E108"),sQuery(id+"F0.wireOp",EDGE,"E109"),sQuery(id+"F0.wireOp",EDGE,"E110"),sQuery(id+"F0.wireOp",EDGE,"E111"),sQuery(id+"F0.wireOp",EDGE,"E112"),sQuery(id+"F0.wireOp",EDGE,"E113"),sQuery(id+"F0.wireOp",EDGE,"E114"),sQuery(id+"F0.wireOp",EDGE,"E115"),sQuery(id+"F0.wireOp",EDGE,"E116"),sQuery(id+"F0.wireOp",EDGE,"E117"),sQuery(id+"F0.wireOp",EDGE,"E118"),sQuery(id+"F0.wireOp",EDGE,"E119"),sQuery(id+"F0.wireOp",EDGE,"E120"),sQuery(id+"F0.wireOp",EDGE,"E121"),sQuery(id+"F0.wireOp",EDGE,"E122"),sQuery(id+"F0.wireOp",EDGE,"E123"),sQuery(id+"F0.wireOp",EDGE,"E124"),sQuery(id+"F0.wireOp",EDGE,"E125"),sQuery(id+"F0.wireOp",EDGE,"E126"),sQuery(id+"F0.wireOp",EDGE,"E127"),sQuery(id+"F0.wireOp",EDGE,"E128"),sQuery(id+"F0.wireOp",EDGE,"E129"),sQuery(id+"F0.wireOp",EDGE,"E130"),sQuery(id+"F0.wireOp",EDGE,"E131"),sQuery(id+"F0.wireOp",EDGE,"E132"),sQuery(id+"F0.wireOp",EDGE,"E133"),sQuery(id+"F0.wireOp",EDGE,"E134"),sQuery(id+"F0.wireOp",EDGE,"E135"),sQuery(id+"F0.wireOp",EDGE,"E136"),sQuery(id+"F0.wireOp",EDGE,"E137"),sQuery(id+"F0.wireOp",EDGE,"E138"),sQuery(id+"F0.wireOp",EDGE,"E139"),sQuery(id+"F0.wireOp",EDGE,"E140"),sQuery(id+"F0.wireOp",EDGE,"E141"),sQuery(id+"F0.wireOp",EDGE,"E142"),sQuery(id+"F0.wireOp",EDGE,"E143"),sQuery(id+"F0.wireOp",EDGE,"E144"),sQuery(id+"F0.wireOp",EDGE,"E145"),sQuery(id+"F0.wireOp",EDGE,"E146"),sQuery(id+"F0.wireOp",EDGE,"E147"),sQuery(id+"F0.wireOp",EDGE,"E148"),sQuery(id+"F0.wireOp",EDGE,"E149"),sQuery(id+"F0.wireOp",EDGE,"E150"),sQuery(id+"F0.wireOp",EDGE,"E151"),sQuery(id+"F0.wireOp",EDGE,"E152"),sQuery(id+"F0.wireOp",EDGE,"E153"),sQuery(id+"F0.wireOp",EDGE,"E154"),sQuery(id+"F0.wireOp",EDGE,"E155"),sQuery(id+"F0.wireOp",EDGE,"E156"),sQuery(id+"F0.wireOp",EDGE,"E157"),sQuery(id+"F0.wireOp",EDGE,"E158"),sQuery(id+"F0.wireOp",EDGE,"E159"),sQuery(id+"F0.wireOp",EDGE,"E160"),sQuery(id+"F0.wireOp",EDGE,"E161"),sQuery(id+"F0.wireOp",EDGE,"E162"),sQuery(id+"F0.wireOp",EDGE,"E163"),sQuery(id+"F0.wireOp",EDGE,"E164"),sQuery(id+"F0.wireOp",EDGE,"E165"),sQuery(id+"F0.wireOp",EDGE,"E166"),sQuery(id+"F0.wireOp",EDGE,"E167"),sQuery(id+"F0.wireOp",EDGE,"E168"),sQuery(id+"F0.wireOp",EDGE,"E169"),sQuery(id+"F0.wireOp",EDGE,"E170"),sQuery(id+"F0.wireOp",EDGE,"E171"),sQuery(id+"F0.wireOp",EDGE,"E172"),sQuery(id+"F0.wireOp",EDGE,"E173"),sQuery(id+"F0.wireOp",EDGE,"E174"),sQuery(id+"F0.wireOp",EDGE,"E175"),sQuery(id+"F0.wireOp",EDGE,"E176"),sQuery(id+"F0.wireOp",EDGE,"E177"),sQuery(id+"F0.wireOp",EDGE,"E178"),sQuery(id+"F0.wireOp",EDGE,"E179"),sQuery(id+"F0.wireOp",EDGE,"E180"),sQuery(id+"F0.wireOp",EDGE,"E181"),sQuery(id+"F0.wireOp",EDGE,"E182"),sQuery(id+"F0.wireOp",EDGE,"E183"),sQuery(id+"F0.wireOp",EDGE,"E184"),sQuery(id+"F0.wireOp",EDGE,"E185"),sQuery(id+"F0.wireOp",EDGE,"E186"),sQuery(id+"F0.wireOp",EDGE,"E187"),sQuery(id+"F0.wireOp",EDGE,"E188"),sQuery(id+"F0.wireOp",EDGE,"E189"),sQuery(id+"F0.wireOp",EDGE,"E190"),sQuery(id+"F0.wireOp",EDGE,"E191"),sQuery(id+"F0.wireOp",EDGE,"E192"),sQuery(id+"F0.wireOp",EDGE,"E193"),sQuery(id+"F0.wireOp",EDGE,"E194"),sQuery(id+"F0.wireOp",EDGE,"E195"),sQuery(id+"F0.wireOp",EDGE,"E196"),sQuery(id+"F0.wireOp",EDGE,"E197"),sQuery(id+"F0.wireOp",EDGE,"E198"),sQuery(id+"F0.wireOp",EDGE,"E199"),sQuery(id+"F0.wireOp",EDGE,"E200"),sQuery(id+"F0.wireOp",EDGE,"E201"),sQuery(id+"F0.wireOp",EDGE,"E202"),sQuery(id+"F0.wireOp",EDGE,"E203"),sQuery(id+"F0.wireOp",EDGE,"E204"),sQuery(id+"F0.wireOp",EDGE,"E205"),sQuery(id+"F0.wireOp",EDGE,"E206"),sQuery(id+"F0.wireOp",EDGE,"E207"),sQuery(id+"F0.wireOp",EDGE,"E208"),sQuery(id+"F0.wireOp",EDGE,"E209"),sQuery(id+"F0.wireOp",EDGE,"E210"),sQuery(id+"F0.wireOp",EDGE,"E211"),sQuery(id+"F0.wireOp",EDGE,"E212"),sQuery(id+"F0.wireOp",EDGE,"E213"),sQuery(id+"F0.wireOp",EDGE,"E214"),sQuery(id+"F0.wireOp",EDGE,"E215"),sQuery(id+"F0.wireOp",EDGE,"E216"),sQuery(id+"F0.wireOp",EDGE,"E217"),sQuery(id+"F0.wireOp",EDGE,"E218"),sQuery(id+"F0.wireOp",EDGE,"E219"),sQuery(id+"F0.wireOp",EDGE,"E220"),sQuery(id+"F0.wireOp",EDGE,"E221"),sQuery(id+"F0.wireOp",EDGE,"E222"),sQuery(id+"F0.wireOp",EDGE,"E223"),sQuery(id+"F0.wireOp",EDGE,"E224"),sQuery(id+"F0.wireOp",EDGE,"E225"),sQuery(id+"F0.wireOp",EDGE,"E226"),sQuery(id+"F0.wireOp",EDGE,"E227"),sQuery(id+"F0.wireOp",EDGE,"E228"),sQuery(id+"F0.wireOp",EDGE,"E229"),sQuery(id+"F0.wireOp",EDGE,"E230"),sQuery(id+"F0.wireOp",EDGE,"E231"),sQuery(id+"F0.wireOp",EDGE,"E232"),sQuery(id+"F0.wireOp",EDGE,"E233"),sQuery(id+"F0.wireOp",EDGE,"E234"),sQuery(id+"F0.wireOp",EDGE,"E235"),sQuery(id+"F0.wireOp",EDGE,"E236"),sQuery(id+"F0.wireOp",EDGE,"E237"),sQuery(id+"F0.wireOp",EDGE,"E238"),sQuery(id+"F0.wireOp",EDGE,"E239"),sQuery(id+"F0.wireOp",EDGE,"E240"),sQuery(id+"F0.wireOp",EDGE,"E241"),sQuery(id+"F0.wireOp",EDGE,"E242"),sQuery(id+"F0.wireOp",EDGE,"E243"),sQuery(id+"F0.wireOp",EDGE,"E244"),sQuery(id+"F0.wireOp",EDGE,"E245"),sQuery(id+"F0.wireOp",EDGE,"E246"),sQuery(id+"F0.wireOp",EDGE,"E247"),sQuery(id+"F0.wireOp",EDGE,"E248"),sQuery(id+"F0.wireOp",EDGE,"E249"),sQuery(id+"F0.wireOp",EDGE,"E250"),sQuery(id+"F0.wireOp",EDGE,"E251"),sQuery(id+"F0.wireOp",EDGE,"E252"),sQuery(id+"F0.wireOp",EDGE,"E253"),sQuery(id+"F0.wireOp",EDGE,"E254"),sQuery(id+"F0.wireOp",EDGE,"E255"),sQuery(id+"F0.wireOp",EDGE,"E256"),sQuery(id+"F0.wireOp",EDGE,"E257"),sQuery(id+"F0.wireOp",EDGE,"E258"),sQuery(id+"F0.wireOp",EDGE,"E259"),sQuery(id+"F0.wireOp",EDGE,"E260"),sQuery(id+"F0.wireOp",EDGE,"E261"),sQuery(id+"F0.wireOp",EDGE,"E262"),sQuery(id+"F0.wireOp",EDGE,"E263"),sQuery(id+"F0.wireOp",EDGE,"E264"),sQuery(id+"F0.wireOp",EDGE,"E265"),sQuery(id+"F0.wireOp",EDGE,"E266"),sQuery(id+"F0.wireOp",EDGE,"E267"),sQuery(id+"F0.wireOp",EDGE,"E268"),sQuery(id+"F0.wireOp",EDGE,"E269"),sQuery(id+"F0.wireOp",EDGE,"E270"),sQuery(id+"F0.wireOp",EDGE,"E271"),sQuery(id+"F0.wireOp",EDGE,"E272"),sQuery(id+"F0.wireOp",EDGE,"E273"),sQuery(id+"F0.wireOp",EDGE,"E274"),sQuery(id+"F0.wireOp",EDGE,"E275"),sQuery(id+"F0.wireOp",EDGE,"E276"),sQuery(id+"F0.wireOp",EDGE,"E277"),sQuery(id+"F0.wireOp",EDGE,"E278"),sQuery(id+"F0.wireOp",EDGE,"E279"),sQuery(id+"F0.wireOp",EDGE,"E280"),sQuery(id+"F0.wireOp",EDGE,"E281"),sQuery(id+"F0.wireOp",EDGE,"E282"),sQuery(id+"F0.wireOp",EDGE,"E283"),sQuery(id+"F0.wireOp",EDGE,"E284"),sQuery(id+"F0.wireOp",EDGE,"E285"),sQuery(id+"F0.wireOp",EDGE,"E286"),sQuery(id+"F0.wireOp",EDGE,"E287"),sQuery(id+"F0.wireOp",EDGE,"E288"),sQuery(id+"F0.wireOp",EDGE,"E289"),sQuery(id+"F0.wireOp",EDGE,"E290"),sQuery(id+"F0.wireOp",EDGE,"E291"),sQuery(id+"F0.wireOp",EDGE,"E292"),sQuery(id+"F0.wireOp",EDGE,"E293"),sQuery(id+"F0.wireOp",EDGE,"E294"),sQuery(id+"F0.wireOp",EDGE,"E295"),sQuery(id+"F0.wireOp",EDGE,"E296"),sQuery(id+"F0.wireOp",EDGE,"E297"),sQuery(id+"F0.wireOp",EDGE,"E298"),sQuery(id+"F0.wireOp",EDGE,"E299"),sQuery(id+"F0.wireOp",EDGE,"E300"),sQuery(id+"F0.wireOp",EDGE,"E301"),sQuery(id+"F0.wireOp",EDGE,"E302"),sQuery(id+"F0.wireOp",EDGE,"E303"),sQuery(id+"F0.wireOp",EDGE,"E304"),sQuery(id+"F0.wireOp",EDGE,"E305"),sQuery(id+"F0.wireOp",EDGE,"E306"),sQuery(id+"F0.wireOp",EDGE,"E307"),sQuery(id+"F0.wireOp",EDGE,"E308"),sQuery(id+"F0.wireOp",EDGE,"E309"),sQuery(id+"F0.wireOp",EDGE,"E310"),sQuery(id+"F0.wireOp",EDGE,"E311"),sQuery(id+"F0.wireOp",EDGE,"E312"),sQuery(id+"F0.wireOp",EDGE,"E313"),sQuery(id+"F0.wireOp",EDGE,"E314"),sQuery(id+"F0.wireOp",EDGE,"E315"),sQuery(id+"F0.wireOp",EDGE,"E316"),sQuery(id+"F0.wireOp",EDGE,"E317"),sQuery(id+"F0.wireOp",EDGE,"E318"),sQuery(id+"F0.wireOp",EDGE,"E319"),sQuery(id+"F0.wireOp",EDGE,"E320"),sQuery(id+"F0.wireOp",EDGE,"E321"),sQuery(id+"F0.wireOp",EDGE,"E322"),sQuery(id+"F0.wireOp",EDGE,"E323"),sQuery(id+"F0.wireOp",EDGE,"E324"),sQuery(id+"F0.wireOp",EDGE,"E325"),sQuery(id+"F0.wireOp",EDGE,"E326"),sQuery(id+"F0.wireOp",EDGE,"E327"),sQuery(id+"F0.wireOp",EDGE,"E328"),sQuery(id+"F0.wireOp",EDGE,"E329"),sQuery(id+"F0.wireOp",EDGE,"E330"),sQuery(id+"F0.wireOp",EDGE,"E331"),sQuery(id+"F0.wireOp",EDGE,"E332"),sQuery(id+"F0.wireOp",EDGE,"E333"),sQuery(id+"F0.wireOp",EDGE,"E334"),sQuery(id+"F0.wireOp",EDGE,"E335"),sQuery(id+"F0.wireOp",EDGE,"E336"),sQuery(id+"F0.wireOp",EDGE,"E337"),sQuery(id+"F0.wireOp",EDGE,"E338"),sQuery(id+"F0.wireOp",EDGE,"E339"),sQuery(id+"F0.wireOp",EDGE,"E340"),sQuery(id+"F0.wireOp",EDGE,"E341"),sQuery(id+"F0.wireOp",EDGE,"E342"),sQuery(id+"F0.wireOp",EDGE,"E343"),sQuery(id+"F0.wireOp",EDGE,"E344"),sQuery(id+"F0.wireOp",EDGE,"E345"),sQuery(id+"F0.wireOp",EDGE,"E346"),sQuery(id+"F0.wireOp",EDGE,"E347"),sQuery(id+"F0.wireOp",EDGE,"E348"),sQuery(id+"F0.wireOp",EDGE,"E349"),sQuery(id+"F0.wireOp",EDGE,"E350"),sQuery(id+"F0.wireOp",EDGE,"E351"),sQuery(id+"F0.wireOp",EDGE,"E352"),sQuery(id+"F0.wireOp",EDGE,"E353"),sQuery(id+"F0.wireOp",EDGE,"E354"),sQuery(id+"F0.wireOp",EDGE,"E355"),sQuery(id+"F0.wireOp",EDGE,"E356"),sQuery(id+"F0.wireOp",EDGE,"E357"),sQuery(id+"F0.wireOp",EDGE,"E358"),sQuery(id+"F0.wireOp",EDGE,"E359"),sQuery(id+"F0.wireOp",EDGE,"E360"),sQuery(id+"F0.wireOp",EDGE,"E361"),sQuery(id+"F0.wireOp",EDGE,"E362"),sQuery(id+"F0.wireOp",EDGE,"E363"),sQuery(id+"F0.wireOp",EDGE,"E364"),sQuery(id+"F0.wireOp",EDGE,"E365"),sQuery(id+"F0.wireOp",EDGE,"E366"),sQuery(id+"F0.wireOp",EDGE,"E367"),sQuery(id+"F0.wireOp",EDGE,"E368"),sQuery(id+"F0.wireOp",EDGE,"E369"),sQuery(id+"F0.wireOp",EDGE,"E370"),sQuery(id+"F0.wireOp",EDGE,"E371"),sQuery(id+"F0.wireOp",EDGE,"E372"),sQuery(id+"F0.wireOp",EDGE,"E373"),sQuery(id+"F0.wireOp",EDGE,"E374"),sQuery(id+"F0.wireOp",EDGE,"E375"),sQuery(id+"F0.wireOp",EDGE,"E376"),sQuery(id+"F0.wireOp",EDGE,"E377"),sQuery(id+"F0.wireOp",EDGE,"E378"),sQuery(id+"F0.wireOp",EDGE,"E379"),sQuery(id+"F0.wireOp",EDGE,"E380"),sQuery(id+"F0.wireOp",EDGE,"E381"),sQuery(id+"F0.wireOp",EDGE,"E382"),sQuery(id+"F0.wireOp",EDGE,"E383"),sQuery(id+"F0.wireOp",EDGE,"E384"),sQuery(id+"F0.wireOp",EDGE,"E385"),sQuery(id+"F0.wireOp",EDGE,"E386"),sQuery(id+"F0.wireOp",EDGE,"E387"),sQuery(id+"F0.wireOp",EDGE,"E388"),sQuery(id+"F0.wireOp",EDGE,"E389"),sQuery(id+"F0.wireOp",EDGE,"E390"),sQuery(id+"F0.wireOp",EDGE,"E391"),sQuery(id+"F0.wireOp",EDGE,"E392"),sQuery(id+"F0.wireOp",EDGE,"E393"),sQuery(id+"F0.wireOp",EDGE,"E394"),sQuery(id+"F0.wireOp",EDGE,"E395"),sQuery(id+"F0.wireOp",EDGE,"E396"),sQuery(id+"F0.wireOp",EDGE,"E397"),sQuery(id+"F0.wireOp",EDGE,"E398"),sQuery(id+"F0.wireOp",EDGE,"E399"),sQuery(id+"F0.wireOp",EDGE,"E400"),sQuery(id+"F0.wireOp",EDGE,"E401"),sQuery(id+"F0.wireOp",EDGE,"E402"),sQuery(id+"F0.wireOp",EDGE,"E403"),sQuery(id+"F0.wireOp",EDGE,"E404"),sQuery(id+"F0.wireOp",EDGE,"E405"),sQuery(id+"F0.wireOp",EDGE,"E406"),sQuery(id+"F0.wireOp",EDGE,"E407"),sQuery(id+"F0.wireOp",EDGE,"E408"),sQuery(id+"F0.wireOp",EDGE,"E409"),sQuery(id+"F0.wireOp",EDGE,"E410"),sQuery(id+"F0.wireOp",EDGE,"E411"),sQuery(id+"F0.wireOp",EDGE,"E412"),sQuery(id+"F0.wireOp",EDGE,"E413"),sQuery(id+"F0.wireOp",EDGE,"E414"),sQuery(id+"F0.wireOp",EDGE,"E417"),sQuery(id+"F0.wireOp",EDGE,"E419"),sQuery(id+"F0.wireOp",EDGE,"E422"),sQuery(id+"F0.wireOp",EDGE,"E423"),sQuery(id+"F0.wireOp",EDGE,"E424"),sQuery(id+"F0.wireOp",EDGE,"E425"),sQuery(id+"F0.wireOp",EDGE,"E426"),sQuery(id+"F0.wireOp",EDGE,"E427")])],"isStart":true});
            var Q2;
            Q2=makeQuery(id+"F3.opExtrude","CAP_EDGE",EDGE,{"disambiguationData":[OSD([sQuery(id+"F0.wireOp",EDGE,"E417")])],"isStart":true});
            fillet(context, id + "F4", {"entities" : qUnion([Q0, Q1, Q2]), "radius" : 0.3 * mm, "allowEdgeOverflow" : false});
        }
        {
            var Q0;
            Q0=makeQuery(id+"F0.imprint","IMPRINT",FACE,{"disambiguationData":[TD([[makeQuery(id+"F0.imprint","IMPRINT",EDGE,{"derivedFrom":sQuery(id+"F0.wireOp",EDGE,"E418")}),1.0]])]});
            extrude(context, id + "F5", {"entities" : qUnion([Q0]), "operationType" : NewBodyOperationType.ADD, "depth" : 6 * mm, "offsetDistance" : 25 * mm, "hasSecondDirection" : true, "secondDirectionOppositeDirection" : true, "secondDirectionDepth" : 0 * mm});
        }
        {
            var Q0;
            Q0=makeQuery(id+"F5.opExtrude","CAP_FACE",FACE,{"disambiguationData":[OSD([sQuery(id+"F0.wireOp",EDGE,"E418")])],"isStart":true});
            var sketch = newSketch(context, id + "F6", { "sketchPlane" : qUnion([Q0])});
            skCircle(sketch, "E428", {"center": v(0, 0) * mm, "radius": 1.73 * mm});
            skSolve(sketch);
        }
        {
            var Q0;
            Q0=makeQuery(id+"F6.imprint","IMPRINT",FACE,{"disambiguationData":[TD([[makeQuery(id+"F6.imprint","IMPRINT",EDGE,{"derivedFrom":sQuery(id+"F6.wireOp",EDGE,"E428")}),1.0]])]});
            extrude(context, id + "F7", {"entities" : qUnion([Q0]), "operationType" : NewBodyOperationType.REMOVE, "oppositeDirection" : true, "depth" : 25 * mm, "offsetDistance" : 25 * mm});
        }
    });
